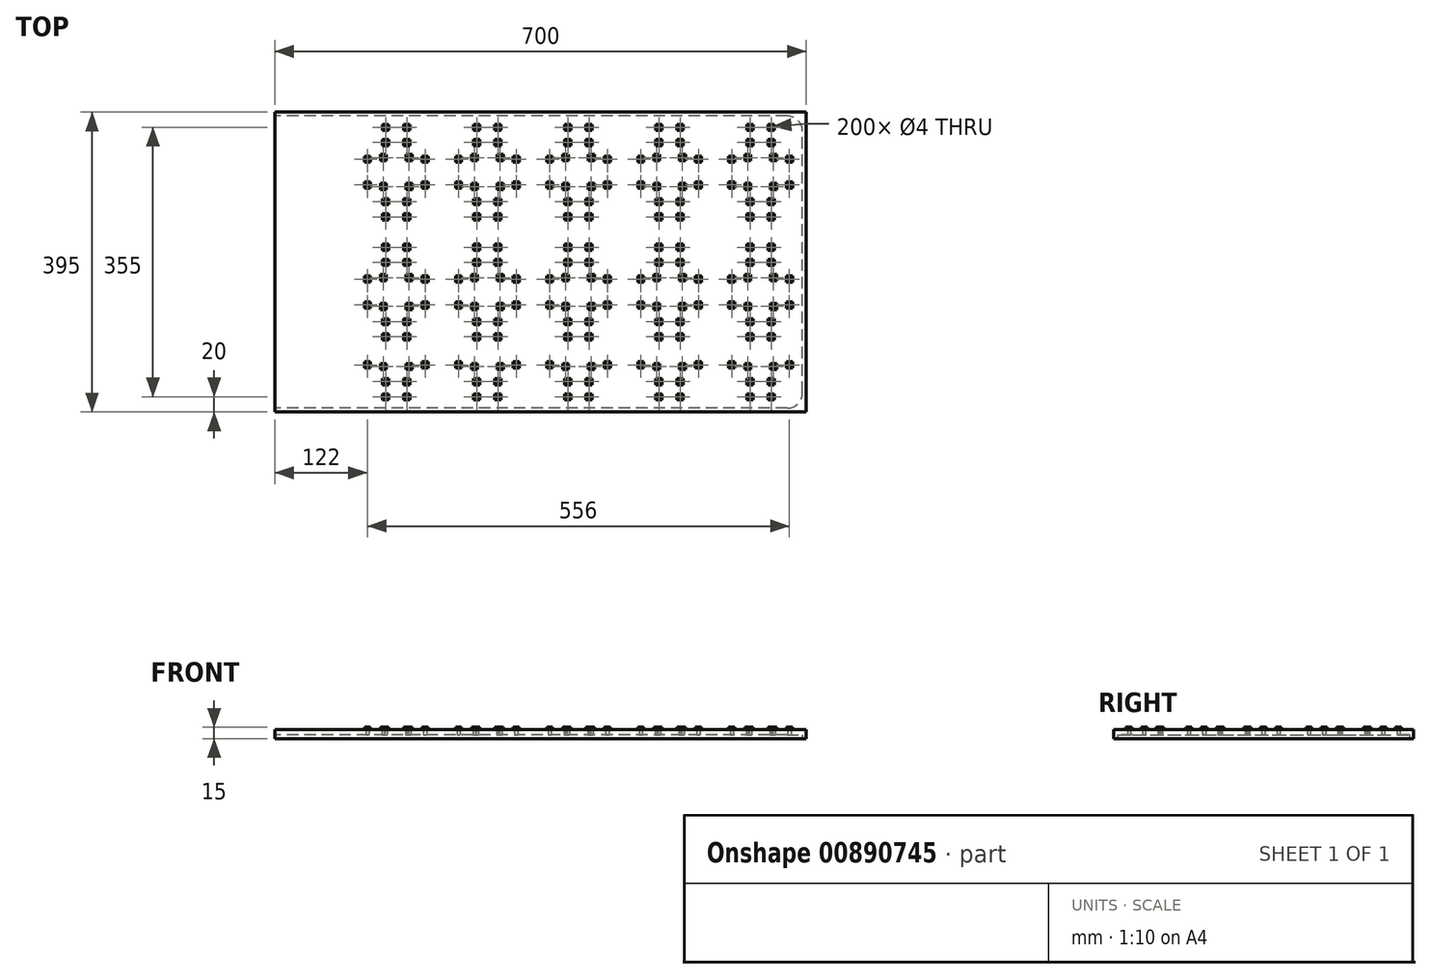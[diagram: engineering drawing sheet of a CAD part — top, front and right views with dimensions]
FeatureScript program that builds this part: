
annotation { "Feature Type Name" : "Feature", "Feature Type Description" : "" }
export const myFeature = defineFeature(function(context is Context, id is Id, definition is map)
    precondition{}
    {
        {
            var Q0;
            Q0=qCreatedBy(makeId("Top.planeOp"),FACE);
            var sketch = newSketch(context, id + "F0", { "sketchPlane" : qUnion([Q0])});
            skLineSegment(sketch, "E0.bottom", {"start": v(0, 0) * mm, "end": v(-700, 0) * mm});
            skLineSegment(sketch, "E0.top", {"start": v(0, 395) * mm, "end": v(-700, 395) * mm});
            skLineSegment(sketch, "E0.left", {"start": v(0, 0) * mm, "end": v(0, 395) * mm});
            skLineSegment(sketch, "E0.right", {"start": v(-700, 0) * mm, "end": v(-700, 395) * mm});
            skPoint(sketch, "E1", {"position": v(-46, 40) * mm});
            skPoint(sketch, "E2", {"position": v(-46, 20) * mm});
            skPoint(sketch, "E3", {"position": v(-43, 60) * mm});
            skPoint(sketch, "E4", {"position": v(-22, 62) * mm});
            skLineSegment(sketch, "E5", {"start": v(0, 79) * mm, "end": v(-60, 79) * mm, "construction": true});
            skLineSegment(sketch, "E6", {"start": v(-60, 79) * mm, "end": v(-60, 0) * mm, "construction": true});
            skLineSegment(sketch, "E7", {"start": v(0, 158) * mm, "end": v(-60, 158) * mm, "construction": true});
            skLineSegment(sketch, "E8", {"start": v(0, 237) * mm, "end": v(-60, 237) * mm, "construction": true});
            skLineSegment(sketch, "E9", {"start": v(0, 316) * mm, "end": v(-60, 316) * mm, "construction": true});
            skLineSegment(sketch, "E10.0.1.2", {"start": v(0, 395) * mm, "end": v(-60, 395) * mm});
            skPoint(sketch, "E10.0.1.3", {"position": v(-46, 119) * mm});
            skPoint(sketch, "E10.0.1.4", {"position": v(-43, 139) * mm});
            skPoint(sketch, "E10.0.1.5", {"position": v(-46, 99) * mm});
            skPoint(sketch, "E10.0.1.6", {"position": v(-22, 141) * mm});
            skLineSegment(sketch, "E10.direction1", {"start": v(-46, 20) * mm, "end": v(-21, 20) * mm, "construction": true});
            skLineSegment(sketch, "E10.direction2", {"start": v(-46, 20) * mm, "end": v(-46, 99) * mm, "construction": true});
            skPoint(sketch, "E11.MirrorP", {"position": v(-43, 177) * mm});
            skPoint(sketch, "E12.MirrorP", {"position": v(-46, 217) * mm});
            skPoint(sketch, "E13.MirrorP", {"position": v(-46, 197) * mm});
            skPoint(sketch, "E14.MirrorP", {"position": v(-22, 175) * mm});
            skPoint(sketch, "E15.MirrorP", {"position": v(-43, 297) * mm});
            skPoint(sketch, "E16.MirrorP", {"position": v(-43, 335) * mm});
            skPoint(sketch, "E17.MirrorP", {"position": v(-46, 257) * mm});
            skPoint(sketch, "E18.MirrorP", {"position": v(-46, 277) * mm});
            skPoint(sketch, "E19.MirrorP", {"position": v(-46, 375) * mm});
            skPoint(sketch, "E20.MirrorP", {"position": v(-46, 355) * mm});
            skPoint(sketch, "E21.MirrorP", {"position": v(-22, 299) * mm});
            skPoint(sketch, "E22.MirrorP", {"position": v(-22, 333) * mm});
            skPoint(sketch, "E23.MirrorP", {"position": v(-74, 40) * mm});
            skPoint(sketch, "E24.MirrorP", {"position": v(-98, 62) * mm});
            skPoint(sketch, "E25.MirrorP", {"position": v(-77, 60) * mm});
            skPoint(sketch, "E26.MirrorP", {"position": v(-74, 20) * mm});
            skPoint(sketch, "E27.MirrorP", {"position": v(-74, 99) * mm});
            skPoint(sketch, "E28.MirrorP", {"position": v(-74, 375) * mm});
            skPoint(sketch, "E29.MirrorP", {"position": v(-77, 177) * mm});
            skPoint(sketch, "E30.MirrorP", {"position": v(-77, 335) * mm});
            skPoint(sketch, "E31.MirrorP", {"position": v(-98, 141) * mm});
            skPoint(sketch, "E32.MirrorP", {"position": v(-74, 355) * mm});
            skPoint(sketch, "E33.MirrorP", {"position": v(-77, 297) * mm});
            skPoint(sketch, "E34.MirrorP", {"position": v(-74, 257) * mm});
            skPoint(sketch, "E35.MirrorP", {"position": v(-98, 333) * mm});
            skPoint(sketch, "E36.MirrorP", {"position": v(-74, 217) * mm});
            skPoint(sketch, "E37.MirrorP", {"position": v(-98, 299) * mm});
            skPoint(sketch, "E38.MirrorP", {"position": v(-74, 277) * mm});
            skPoint(sketch, "E39.MirrorP", {"position": v(-98, 175) * mm});
            skPoint(sketch, "E40.MirrorP", {"position": v(-77, 139) * mm});
            skPoint(sketch, "E41.MirrorP", {"position": v(-74, 119) * mm});
            skPoint(sketch, "E42.MirrorP", {"position": v(-74, 197) * mm});
            skPoint(sketch, "E43.1.0.0", {"position": v(-218, 299) * mm});
            skPoint(sketch, "E43.1.0.1", {"position": v(-142, 299) * mm});
            skPoint(sketch, "E43.1.0.2", {"position": v(-194, 40) * mm});
            skPoint(sketch, "E43.1.0.3", {"position": v(-218, 175) * mm});
            skPoint(sketch, "E43.1.0.4", {"position": v(-218, 333) * mm});
            skPoint(sketch, "E43.1.0.5", {"position": v(-166, 197) * mm});
            skPoint(sketch, "E43.1.0.6", {"position": v(-197, 297) * mm});
            skPoint(sketch, "E43.1.0.7", {"position": v(-197, 335) * mm});
            skPoint(sketch, "E43.1.0.8", {"position": v(-142, 333) * mm});
            skPoint(sketch, "E43.1.0.9", {"position": v(-194, 375) * mm});
            skPoint(sketch, "E43.1.0.10", {"position": v(-163, 60) * mm});
            skPoint(sketch, "E43.1.0.11", {"position": v(-194, 197) * mm});
            skPoint(sketch, "E43.1.0.12", {"position": v(-163, 297) * mm});
            skPoint(sketch, "E43.1.0.13", {"position": v(-166, 375) * mm});
            skPoint(sketch, "E43.1.0.14", {"position": v(-197, 60) * mm});
            skPoint(sketch, "E43.1.0.15", {"position": v(-197, 139) * mm});
            skPoint(sketch, "E43.1.0.16", {"position": v(-166, 99) * mm});
            skPoint(sketch, "E43.1.0.17", {"position": v(-163, 335) * mm});
            skPoint(sketch, "E43.1.0.18", {"position": v(-142, 141) * mm});
            skPoint(sketch, "E43.1.0.19", {"position": v(-163, 177) * mm});
            skPoint(sketch, "E43.1.0.20", {"position": v(-166, 40) * mm});
            skPoint(sketch, "E43.1.0.21", {"position": v(-194, 217) * mm});
            skPoint(sketch, "E43.1.0.22", {"position": v(-194, 99) * mm});
            skPoint(sketch, "E43.1.0.23", {"position": v(-163, 139) * mm});
            skPoint(sketch, "E43.1.0.24", {"position": v(-218, 62) * mm});
            skPoint(sketch, "E43.1.0.25", {"position": v(-197, 177) * mm});
            skPoint(sketch, "E43.1.0.26", {"position": v(-194, 20) * mm});
            skPoint(sketch, "E43.1.0.27", {"position": v(-142, 175) * mm});
            skPoint(sketch, "E43.1.0.28", {"position": v(-166, 257) * mm});
            skPoint(sketch, "E43.1.0.29", {"position": v(-194, 355) * mm});
            skPoint(sketch, "E43.1.0.30", {"position": v(-166, 355) * mm});
            skPoint(sketch, "E43.1.0.31", {"position": v(-194, 277) * mm});
            skPoint(sketch, "E43.1.0.32", {"position": v(-166, 20) * mm});
            skPoint(sketch, "E43.1.0.33", {"position": v(-194, 119) * mm});
            skPoint(sketch, "E43.1.0.34", {"position": v(-166, 217) * mm});
            skPoint(sketch, "E43.1.0.35", {"position": v(-142, 62) * mm});
            skPoint(sketch, "E43.1.0.36", {"position": v(-166, 119) * mm});
            skPoint(sketch, "E43.1.0.37", {"position": v(-218, 141) * mm});
            skPoint(sketch, "E43.1.0.38", {"position": v(-194, 257) * mm});
            skPoint(sketch, "E43.1.0.39", {"position": v(-166, 277) * mm});
            skPoint(sketch, "E43.2.0.0", {"position": v(-338, 299) * mm});
            skPoint(sketch, "E43.2.0.1", {"position": v(-262, 299) * mm});
            skPoint(sketch, "E43.2.0.2", {"position": v(-314, 40) * mm});
            skPoint(sketch, "E43.2.0.3", {"position": v(-338, 175) * mm});
            skPoint(sketch, "E43.2.0.4", {"position": v(-338, 333) * mm});
            skPoint(sketch, "E43.2.0.5", {"position": v(-286, 197) * mm});
            skPoint(sketch, "E43.2.0.6", {"position": v(-317, 297) * mm});
            skPoint(sketch, "E43.2.0.7", {"position": v(-317, 335) * mm});
            skPoint(sketch, "E43.2.0.8", {"position": v(-262, 333) * mm});
            skPoint(sketch, "E43.2.0.9", {"position": v(-314, 375) * mm});
            skPoint(sketch, "E43.2.0.10", {"position": v(-283, 60) * mm});
            skPoint(sketch, "E43.2.0.11", {"position": v(-314, 197) * mm});
            skPoint(sketch, "E43.2.0.12", {"position": v(-283, 297) * mm});
            skPoint(sketch, "E43.2.0.13", {"position": v(-286, 375) * mm});
            skPoint(sketch, "E43.2.0.14", {"position": v(-317, 60) * mm});
            skPoint(sketch, "E43.2.0.15", {"position": v(-317, 139) * mm});
            skPoint(sketch, "E43.2.0.16", {"position": v(-286, 99) * mm});
            skPoint(sketch, "E43.2.0.17", {"position": v(-283, 335) * mm});
            skPoint(sketch, "E43.2.0.18", {"position": v(-262, 141) * mm});
            skPoint(sketch, "E43.2.0.19", {"position": v(-283, 177) * mm});
            skPoint(sketch, "E43.2.0.20", {"position": v(-286, 40) * mm});
            skPoint(sketch, "E43.2.0.21", {"position": v(-314, 217) * mm});
            skPoint(sketch, "E43.2.0.22", {"position": v(-314, 99) * mm});
            skPoint(sketch, "E43.2.0.23", {"position": v(-283, 139) * mm});
            skPoint(sketch, "E43.2.0.24", {"position": v(-338, 62) * mm});
            skPoint(sketch, "E43.2.0.25", {"position": v(-317, 177) * mm});
            skPoint(sketch, "E43.2.0.26", {"position": v(-314, 20) * mm});
            skPoint(sketch, "E43.2.0.27", {"position": v(-262, 175) * mm});
            skPoint(sketch, "E43.2.0.28", {"position": v(-286, 257) * mm});
            skPoint(sketch, "E43.2.0.29", {"position": v(-314, 355) * mm});
            skPoint(sketch, "E43.2.0.30", {"position": v(-286, 355) * mm});
            skPoint(sketch, "E43.2.0.31", {"position": v(-314, 277) * mm});
            skPoint(sketch, "E43.2.0.32", {"position": v(-286, 20) * mm});
            skPoint(sketch, "E43.2.0.33", {"position": v(-314, 119) * mm});
            skPoint(sketch, "E43.2.0.34", {"position": v(-286, 217) * mm});
            skPoint(sketch, "E43.2.0.35", {"position": v(-262, 62) * mm});
            skPoint(sketch, "E43.2.0.36", {"position": v(-286, 119) * mm});
            skPoint(sketch, "E43.2.0.37", {"position": v(-338, 141) * mm});
            skPoint(sketch, "E43.2.0.38", {"position": v(-314, 257) * mm});
            skPoint(sketch, "E43.2.0.39", {"position": v(-286, 277) * mm});
            skPoint(sketch, "E43.3.0.0", {"position": v(-458, 299) * mm});
            skPoint(sketch, "E43.3.0.1", {"position": v(-382, 299) * mm});
            skPoint(sketch, "E43.3.0.2", {"position": v(-434, 40) * mm});
            skPoint(sketch, "E43.3.0.3", {"position": v(-458, 175) * mm});
            skPoint(sketch, "E43.3.0.4", {"position": v(-458, 333) * mm});
            skPoint(sketch, "E43.3.0.5", {"position": v(-406, 197) * mm});
            skPoint(sketch, "E43.3.0.6", {"position": v(-437, 297) * mm});
            skPoint(sketch, "E43.3.0.7", {"position": v(-437, 335) * mm});
            skPoint(sketch, "E43.3.0.8", {"position": v(-382, 333) * mm});
            skPoint(sketch, "E43.3.0.9", {"position": v(-434, 375) * mm});
            skPoint(sketch, "E43.3.0.10", {"position": v(-403, 60) * mm});
            skPoint(sketch, "E43.3.0.11", {"position": v(-434, 197) * mm});
            skPoint(sketch, "E43.3.0.12", {"position": v(-403, 297) * mm});
            skPoint(sketch, "E43.3.0.13", {"position": v(-406, 375) * mm});
            skPoint(sketch, "E43.3.0.14", {"position": v(-437, 60) * mm});
            skPoint(sketch, "E43.3.0.15", {"position": v(-437, 139) * mm});
            skPoint(sketch, "E43.3.0.16", {"position": v(-406, 99) * mm});
            skPoint(sketch, "E43.3.0.17", {"position": v(-403, 335) * mm});
            skPoint(sketch, "E43.3.0.18", {"position": v(-382, 141) * mm});
            skPoint(sketch, "E43.3.0.19", {"position": v(-403, 177) * mm});
            skPoint(sketch, "E43.3.0.20", {"position": v(-406, 40) * mm});
            skPoint(sketch, "E43.3.0.21", {"position": v(-434, 217) * mm});
            skPoint(sketch, "E43.3.0.22", {"position": v(-434, 99) * mm});
            skPoint(sketch, "E43.3.0.23", {"position": v(-403, 139) * mm});
            skPoint(sketch, "E43.3.0.24", {"position": v(-458, 62) * mm});
            skPoint(sketch, "E43.3.0.25", {"position": v(-437, 177) * mm});
            skPoint(sketch, "E43.3.0.26", {"position": v(-434, 20) * mm});
            skPoint(sketch, "E43.3.0.27", {"position": v(-382, 175) * mm});
            skPoint(sketch, "E43.3.0.28", {"position": v(-406, 257) * mm});
            skPoint(sketch, "E43.3.0.29", {"position": v(-434, 355) * mm});
            skPoint(sketch, "E43.3.0.30", {"position": v(-406, 355) * mm});
            skPoint(sketch, "E43.3.0.31", {"position": v(-434, 277) * mm});
            skPoint(sketch, "E43.3.0.32", {"position": v(-406, 20) * mm});
            skPoint(sketch, "E43.3.0.33", {"position": v(-434, 119) * mm});
            skPoint(sketch, "E43.3.0.34", {"position": v(-406, 217) * mm});
            skPoint(sketch, "E43.3.0.35", {"position": v(-382, 62) * mm});
            skPoint(sketch, "E43.3.0.36", {"position": v(-406, 119) * mm});
            skPoint(sketch, "E43.3.0.37", {"position": v(-458, 141) * mm});
            skPoint(sketch, "E43.3.0.38", {"position": v(-434, 257) * mm});
            skPoint(sketch, "E43.3.0.39", {"position": v(-406, 277) * mm});
            skPoint(sketch, "E43.4.0.0", {"position": v(-578, 299) * mm});
            skPoint(sketch, "E43.4.0.1", {"position": v(-502, 299) * mm});
            skPoint(sketch, "E43.4.0.2", {"position": v(-554, 40) * mm});
            skPoint(sketch, "E43.4.0.3", {"position": v(-578, 175) * mm});
            skPoint(sketch, "E43.4.0.4", {"position": v(-578, 333) * mm});
            skPoint(sketch, "E43.4.0.5", {"position": v(-526, 197) * mm});
            skPoint(sketch, "E43.4.0.6", {"position": v(-557, 297) * mm});
            skPoint(sketch, "E43.4.0.7", {"position": v(-557, 335) * mm});
            skPoint(sketch, "E43.4.0.8", {"position": v(-502, 333) * mm});
            skPoint(sketch, "E43.4.0.9", {"position": v(-554, 375) * mm});
            skPoint(sketch, "E43.4.0.10", {"position": v(-523, 60) * mm});
            skPoint(sketch, "E43.4.0.11", {"position": v(-554, 197) * mm});
            skPoint(sketch, "E43.4.0.12", {"position": v(-523, 297) * mm});
            skPoint(sketch, "E43.4.0.13", {"position": v(-526, 375) * mm});
            skPoint(sketch, "E43.4.0.14", {"position": v(-557, 60) * mm});
            skPoint(sketch, "E43.4.0.15", {"position": v(-557, 139) * mm});
            skPoint(sketch, "E43.4.0.16", {"position": v(-526, 99) * mm});
            skPoint(sketch, "E43.4.0.17", {"position": v(-523, 335) * mm});
            skPoint(sketch, "E43.4.0.18", {"position": v(-502, 141) * mm});
            skPoint(sketch, "E43.4.0.19", {"position": v(-523, 177) * mm});
            skPoint(sketch, "E43.4.0.20", {"position": v(-526, 40) * mm});
            skPoint(sketch, "E43.4.0.21", {"position": v(-554, 217) * mm});
            skPoint(sketch, "E43.4.0.22", {"position": v(-554, 99) * mm});
            skPoint(sketch, "E43.4.0.23", {"position": v(-523, 139) * mm});
            skPoint(sketch, "E43.4.0.24", {"position": v(-578, 62) * mm});
            skPoint(sketch, "E43.4.0.25", {"position": v(-557, 177) * mm});
            skPoint(sketch, "E43.4.0.26", {"position": v(-554, 20) * mm});
            skPoint(sketch, "E43.4.0.27", {"position": v(-502, 175) * mm});
            skPoint(sketch, "E43.4.0.28", {"position": v(-526, 257) * mm});
            skPoint(sketch, "E43.4.0.29", {"position": v(-554, 355) * mm});
            skPoint(sketch, "E43.4.0.30", {"position": v(-526, 355) * mm});
            skPoint(sketch, "E43.4.0.31", {"position": v(-554, 277) * mm});
            skPoint(sketch, "E43.4.0.32", {"position": v(-526, 20) * mm});
            skPoint(sketch, "E43.4.0.33", {"position": v(-554, 119) * mm});
            skPoint(sketch, "E43.4.0.34", {"position": v(-526, 217) * mm});
            skPoint(sketch, "E43.4.0.35", {"position": v(-502, 62) * mm});
            skPoint(sketch, "E43.4.0.36", {"position": v(-526, 119) * mm});
            skPoint(sketch, "E43.4.0.37", {"position": v(-578, 141) * mm});
            skPoint(sketch, "E43.4.0.38", {"position": v(-554, 257) * mm});
            skPoint(sketch, "E43.4.0.39", {"position": v(-526, 277) * mm});
            skLineSegment(sketch, "E43.direction1", {"start": v(-74, 20) * mm, "end": v(-194, 20) * mm, "construction": true});
            skSolve(sketch);
        }
        {
            var Q0;
            Q0 = qSketchRegion(id + "F0", true);
            extrude(context, id + "F1", {"entities" : qUnion([Q0]), "depth" : 12 * mm, "offsetDistance" : 25 * mm});
        }
        {
            var Q0;
            Q0=makeQuery(id+"F0.imprint","IMPRINT",FACE,{"disambiguationData":[TD([[makeQuery(id+"F0.imprint","IMPRINT",EDGE,{"derivedFrom":sQuery(id+"F0.wireOp",EDGE,"E0.bottom")}),-1.0]])]});
            var sketch = newSketch(context, id + "F2", { "sketchPlane" : qUnion([Q0])});
            skLineSegment(sketch, "E44.bottom", {"start": v(-18, 66) * mm, "end": v(-26, 66) * mm});
            skLineSegment(sketch, "E44.top", {"start": v(-18, 58) * mm, "end": v(-26, 58) * mm});
            skLineSegment(sketch, "E44.left", {"start": v(-18, 66) * mm, "end": v(-18, 58) * mm});
            skLineSegment(sketch, "E44.right", {"start": v(-26, 66) * mm, "end": v(-26, 58) * mm});
            skPoint(sketch, "E44.middle", {"position": v(-22, 62) * mm});
            skLineSegment(sketch, "E45.bottom", {"start": v(-42, 24) * mm, "end": v(-50, 24) * mm});
            skLineSegment(sketch, "E45.top", {"start": v(-42, 16) * mm, "end": v(-50, 16) * mm});
            skLineSegment(sketch, "E45.left", {"start": v(-42, 24) * mm, "end": v(-42, 16) * mm});
            skLineSegment(sketch, "E45.right", {"start": v(-50, 24) * mm, "end": v(-50, 16) * mm});
            skPoint(sketch, "E45.middle", {"position": v(-46, 20) * mm});
            skLineSegment(sketch, "E46.bottom", {"start": v(-42, 44) * mm, "end": v(-50, 44) * mm});
            skLineSegment(sketch, "E46.top", {"start": v(-42, 36) * mm, "end": v(-50, 36) * mm});
            skLineSegment(sketch, "E46.left", {"start": v(-42, 44) * mm, "end": v(-42, 36) * mm});
            skLineSegment(sketch, "E46.right", {"start": v(-50, 44) * mm, "end": v(-50, 36) * mm});
            skPoint(sketch, "E46.middle", {"position": v(-46, 40) * mm});
            skLineSegment(sketch, "E47.bottom", {"start": v(-39, 64) * mm, "end": v(-47, 64) * mm});
            skLineSegment(sketch, "E47.top", {"start": v(-39, 56) * mm, "end": v(-47, 56) * mm});
            skLineSegment(sketch, "E47.left", {"start": v(-39, 64) * mm, "end": v(-39, 56) * mm});
            skLineSegment(sketch, "E47.right", {"start": v(-47, 64) * mm, "end": v(-47, 56) * mm});
            skPoint(sketch, "E47.middle", {"position": v(-43, 60) * mm});
            skLineSegment(sketch, "E48.bottom", {"start": v(-42, 103) * mm, "end": v(-50, 103) * mm});
            skLineSegment(sketch, "E48.top", {"start": v(-42, 95) * mm, "end": v(-50, 95) * mm});
            skLineSegment(sketch, "E48.left", {"start": v(-42, 103) * mm, "end": v(-42, 95) * mm});
            skLineSegment(sketch, "E48.right", {"start": v(-50, 103) * mm, "end": v(-50, 95) * mm});
            skPoint(sketch, "E48.middle", {"position": v(-46, 99) * mm});
            skLineSegment(sketch, "E49.bottom", {"start": v(-42, 123) * mm, "end": v(-50, 123) * mm});
            skLineSegment(sketch, "E49.top", {"start": v(-42, 115) * mm, "end": v(-50, 115) * mm});
            skLineSegment(sketch, "E49.left", {"start": v(-42, 123) * mm, "end": v(-42, 115) * mm});
            skLineSegment(sketch, "E49.right", {"start": v(-50, 123) * mm, "end": v(-50, 115) * mm});
            skPoint(sketch, "E49.middle", {"position": v(-46, 119) * mm});
            skLineSegment(sketch, "E50.bottom", {"start": v(-39, 143) * mm, "end": v(-47, 143) * mm});
            skLineSegment(sketch, "E50.top", {"start": v(-39, 135) * mm, "end": v(-47, 135) * mm});
            skLineSegment(sketch, "E50.left", {"start": v(-39, 143) * mm, "end": v(-39, 135) * mm});
            skLineSegment(sketch, "E50.right", {"start": v(-47, 143) * mm, "end": v(-47, 135) * mm});
            skPoint(sketch, "E50.middle", {"position": v(-43, 139) * mm});
            skLineSegment(sketch, "E51.bottom", {"start": v(-18, 145) * mm, "end": v(-26, 145) * mm});
            skLineSegment(sketch, "E51.top", {"start": v(-18, 137) * mm, "end": v(-26, 137) * mm});
            skLineSegment(sketch, "E51.left", {"start": v(-18, 145) * mm, "end": v(-18, 137) * mm});
            skLineSegment(sketch, "E51.right", {"start": v(-26, 145) * mm, "end": v(-26, 137) * mm});
            skPoint(sketch, "E51.middle", {"position": v(-22, 141) * mm});
            skLineSegment(sketch, "E52.bottom", {"start": v(-18, 179) * mm, "end": v(-26, 179) * mm});
            skLineSegment(sketch, "E52.top", {"start": v(-18, 171) * mm, "end": v(-26, 171) * mm});
            skLineSegment(sketch, "E52.left", {"start": v(-18, 179) * mm, "end": v(-18, 171) * mm});
            skLineSegment(sketch, "E52.right", {"start": v(-26, 179) * mm, "end": v(-26, 171) * mm});
            skPoint(sketch, "E52.middle", {"position": v(-22, 175) * mm});
            skLineSegment(sketch, "E53.bottom", {"start": v(-39, 181) * mm, "end": v(-47, 181) * mm});
            skLineSegment(sketch, "E53.top", {"start": v(-39, 173) * mm, "end": v(-47, 173) * mm});
            skLineSegment(sketch, "E53.left", {"start": v(-39, 181) * mm, "end": v(-39, 173) * mm});
            skLineSegment(sketch, "E53.right", {"start": v(-47, 181) * mm, "end": v(-47, 173) * mm});
            skPoint(sketch, "E53.middle", {"position": v(-43, 177) * mm});
            skLineSegment(sketch, "E54.bottom", {"start": v(-42, 201) * mm, "end": v(-50, 201) * mm});
            skLineSegment(sketch, "E54.top", {"start": v(-42, 193) * mm, "end": v(-50, 193) * mm});
            skLineSegment(sketch, "E54.left", {"start": v(-42, 201) * mm, "end": v(-42, 193) * mm});
            skLineSegment(sketch, "E54.right", {"start": v(-50, 201) * mm, "end": v(-50, 193) * mm});
            skPoint(sketch, "E54.middle", {"position": v(-46, 197) * mm});
            skLineSegment(sketch, "E55.bottom", {"start": v(-42, 221) * mm, "end": v(-50, 221) * mm});
            skLineSegment(sketch, "E55.top", {"start": v(-42, 213) * mm, "end": v(-50, 213) * mm});
            skLineSegment(sketch, "E55.left", {"start": v(-42, 221) * mm, "end": v(-42, 213) * mm});
            skLineSegment(sketch, "E55.right", {"start": v(-50, 221) * mm, "end": v(-50, 213) * mm});
            skPoint(sketch, "E55.middle", {"position": v(-46, 217) * mm});
            skLineSegment(sketch, "E56.bottom", {"start": v(-42, 261) * mm, "end": v(-50, 261) * mm});
            skLineSegment(sketch, "E56.top", {"start": v(-42, 253) * mm, "end": v(-50, 253) * mm});
            skLineSegment(sketch, "E56.left", {"start": v(-42, 261) * mm, "end": v(-42, 253) * mm});
            skLineSegment(sketch, "E56.right", {"start": v(-50, 261) * mm, "end": v(-50, 253) * mm});
            skPoint(sketch, "E56.middle", {"position": v(-46, 257) * mm});
            skLineSegment(sketch, "E57.bottom", {"start": v(-42, 281) * mm, "end": v(-50, 281) * mm});
            skLineSegment(sketch, "E57.top", {"start": v(-42, 273) * mm, "end": v(-50, 273) * mm});
            skLineSegment(sketch, "E57.left", {"start": v(-42, 281) * mm, "end": v(-42, 273) * mm});
            skLineSegment(sketch, "E57.right", {"start": v(-50, 281) * mm, "end": v(-50, 273) * mm});
            skPoint(sketch, "E57.middle", {"position": v(-46, 277) * mm});
            skLineSegment(sketch, "E58.bottom", {"start": v(-39, 301) * mm, "end": v(-47, 301) * mm});
            skLineSegment(sketch, "E58.top", {"start": v(-39, 293) * mm, "end": v(-47, 293) * mm});
            skLineSegment(sketch, "E58.left", {"start": v(-39, 301) * mm, "end": v(-39, 293) * mm});
            skLineSegment(sketch, "E58.right", {"start": v(-47, 301) * mm, "end": v(-47, 293) * mm});
            skPoint(sketch, "E58.middle", {"position": v(-43, 297) * mm});
            skLineSegment(sketch, "E59.bottom", {"start": v(-18, 303) * mm, "end": v(-26, 303) * mm});
            skLineSegment(sketch, "E59.top", {"start": v(-18, 295) * mm, "end": v(-26, 295) * mm});
            skLineSegment(sketch, "E59.left", {"start": v(-18, 303) * mm, "end": v(-18, 295) * mm});
            skLineSegment(sketch, "E59.right", {"start": v(-26, 303) * mm, "end": v(-26, 295) * mm});
            skPoint(sketch, "E59.middle", {"position": v(-22, 299) * mm});
            skLineSegment(sketch, "E60.bottom", {"start": v(-18, 337) * mm, "end": v(-26, 337) * mm});
            skLineSegment(sketch, "E60.top", {"start": v(-18, 329) * mm, "end": v(-26, 329) * mm});
            skLineSegment(sketch, "E60.left", {"start": v(-18, 337) * mm, "end": v(-18, 329) * mm});
            skLineSegment(sketch, "E60.right", {"start": v(-26, 337) * mm, "end": v(-26, 329) * mm});
            skPoint(sketch, "E60.middle", {"position": v(-22, 333) * mm});
            skLineSegment(sketch, "E61.bottom", {"start": v(-39, 339) * mm, "end": v(-47, 339) * mm});
            skLineSegment(sketch, "E61.top", {"start": v(-39, 331) * mm, "end": v(-47, 331) * mm});
            skLineSegment(sketch, "E61.left", {"start": v(-39, 339) * mm, "end": v(-39, 331) * mm});
            skLineSegment(sketch, "E61.right", {"start": v(-47, 339) * mm, "end": v(-47, 331) * mm});
            skPoint(sketch, "E61.middle", {"position": v(-43, 335) * mm});
            skLineSegment(sketch, "E62.bottom", {"start": v(-42, 359) * mm, "end": v(-50, 359) * mm});
            skLineSegment(sketch, "E62.top", {"start": v(-42, 351) * mm, "end": v(-50, 351) * mm});
            skLineSegment(sketch, "E62.left", {"start": v(-42, 359) * mm, "end": v(-42, 351) * mm});
            skLineSegment(sketch, "E62.right", {"start": v(-50, 359) * mm, "end": v(-50, 351) * mm});
            skPoint(sketch, "E62.middle", {"position": v(-46, 355) * mm});
            skLineSegment(sketch, "E63.bottom", {"start": v(-42, 379) * mm, "end": v(-50, 379) * mm});
            skLineSegment(sketch, "E63.top", {"start": v(-42, 371) * mm, "end": v(-50, 371) * mm});
            skLineSegment(sketch, "E63.left", {"start": v(-42, 379) * mm, "end": v(-42, 371) * mm});
            skLineSegment(sketch, "E63.right", {"start": v(-50, 379) * mm, "end": v(-50, 371) * mm});
            skPoint(sketch, "E63.middle", {"position": v(-46, 375) * mm});
            skLineSegment(sketch, "E64.MirrorCS", {"start": v(-81, 143) * mm, "end": v(-73, 143) * mm});
            skLineSegment(sketch, "E65.MirrorCS", {"start": v(-81, 301) * mm, "end": v(-73, 301) * mm});
            skLineSegment(sketch, "E66.MirrorCS", {"start": v(-78, 281) * mm, "end": v(-70, 281) * mm});
            skLineSegment(sketch, "E67.MirrorCS", {"start": v(-81, 143) * mm, "end": v(-81, 135) * mm});
            skLineSegment(sketch, "E68.MirrorCS", {"start": v(-70, 44) * mm, "end": v(-70, 36) * mm});
            skLineSegment(sketch, "E69.MirrorCS", {"start": v(-81, 135) * mm, "end": v(-73, 135) * mm});
            skLineSegment(sketch, "E70.MirrorCS", {"start": v(-70, 281) * mm, "end": v(-70, 273) * mm});
            skLineSegment(sketch, "E71.MirrorCS", {"start": v(-78, 281) * mm, "end": v(-78, 273) * mm});
            skLineSegment(sketch, "E72.MirrorCS", {"start": v(-78, 44) * mm, "end": v(-70, 44) * mm});
            skLineSegment(sketch, "E73.MirrorCS", {"start": v(-78, 273) * mm, "end": v(-70, 273) * mm});
            skLineSegment(sketch, "E74.MirrorCS", {"start": v(-78, 36) * mm, "end": v(-70, 36) * mm});
            skLineSegment(sketch, "E75.MirrorCS", {"start": v(-78, 44) * mm, "end": v(-78, 36) * mm});
            skLineSegment(sketch, "E76.MirrorCS", {"start": v(-73, 143) * mm, "end": v(-73, 135) * mm});
            skLineSegment(sketch, "E77.MirrorCS", {"start": v(-81, 293) * mm, "end": v(-73, 293) * mm});
            skLineSegment(sketch, "E78.MirrorCS", {"start": v(-73, 301) * mm, "end": v(-73, 293) * mm});
            skLineSegment(sketch, "E79.MirrorCS", {"start": v(-81, 301) * mm, "end": v(-81, 293) * mm});
            skLineSegment(sketch, "E80.MirrorCS", {"start": v(-78, 253) * mm, "end": v(-70, 253) * mm});
            skLineSegment(sketch, "E81.MirrorCS", {"start": v(-70, 221) * mm, "end": v(-70, 213) * mm});
            skLineSegment(sketch, "E82.MirrorCS", {"start": v(-78, 261) * mm, "end": v(-70, 261) * mm});
            skLineSegment(sketch, "E83.MirrorCS", {"start": v(-70, 201) * mm, "end": v(-70, 193) * mm});
            skLineSegment(sketch, "E84.MirrorCS", {"start": v(-78, 123) * mm, "end": v(-78, 115) * mm});
            skLineSegment(sketch, "E85.MirrorCS", {"start": v(-78, 371) * mm, "end": v(-70, 371) * mm});
            skLineSegment(sketch, "E86.MirrorCS", {"start": v(-81, 339) * mm, "end": v(-73, 339) * mm});
            skLineSegment(sketch, "E87.MirrorCS", {"start": v(-81, 181) * mm, "end": v(-73, 181) * mm});
            skLineSegment(sketch, "E88.MirrorCS", {"start": v(-78, 351) * mm, "end": v(-70, 351) * mm});
            skLineSegment(sketch, "E89.MirrorCS", {"start": v(-78, 379) * mm, "end": v(-70, 379) * mm});
            skLineSegment(sketch, "E90.MirrorCS", {"start": v(-81, 56) * mm, "end": v(-73, 56) * mm});
            skLineSegment(sketch, "E91.MirrorCS", {"start": v(-81, 331) * mm, "end": v(-73, 331) * mm});
            skLineSegment(sketch, "E92.MirrorCS", {"start": v(-78, 201) * mm, "end": v(-70, 201) * mm});
            skLineSegment(sketch, "E93.MirrorCS", {"start": v(-73, 339) * mm, "end": v(-73, 331) * mm});
            skLineSegment(sketch, "E94.MirrorCS", {"start": v(-70, 24) * mm, "end": v(-70, 16) * mm});
            skLineSegment(sketch, "E95.MirrorCS", {"start": v(-78, 24) * mm, "end": v(-78, 16) * mm});
            skLineSegment(sketch, "E96.MirrorCS", {"start": v(-78, 213) * mm, "end": v(-70, 213) * mm});
            skLineSegment(sketch, "E97.MirrorCS", {"start": v(-78, 103) * mm, "end": v(-78, 95) * mm});
            skLineSegment(sketch, "E98.MirrorCS", {"start": v(-78, 261) * mm, "end": v(-78, 253) * mm});
            skLineSegment(sketch, "E99.MirrorCS", {"start": v(-78, 115) * mm, "end": v(-70, 115) * mm});
            skLineSegment(sketch, "E100.MirrorCS", {"start": v(-81, 173) * mm, "end": v(-73, 173) * mm});
            skLineSegment(sketch, "E101.MirrorCS", {"start": v(-70, 359) * mm, "end": v(-70, 351) * mm});
            skLineSegment(sketch, "E102.MirrorCS", {"start": v(-78, 103) * mm, "end": v(-70, 103) * mm});
            skLineSegment(sketch, "E103.MirrorCS", {"start": v(-70, 123) * mm, "end": v(-70, 115) * mm});
            skLineSegment(sketch, "E104.MirrorCS", {"start": v(-73, 64) * mm, "end": v(-73, 56) * mm});
            skLineSegment(sketch, "E105.MirrorCS", {"start": v(-78, 123) * mm, "end": v(-70, 123) * mm});
            skLineSegment(sketch, "E106.MirrorCS", {"start": v(-70, 379) * mm, "end": v(-70, 371) * mm});
            skLineSegment(sketch, "E107.MirrorCS", {"start": v(-78, 201) * mm, "end": v(-78, 193) * mm});
            skLineSegment(sketch, "E108.MirrorCS", {"start": v(-73, 181) * mm, "end": v(-73, 173) * mm});
            skLineSegment(sketch, "E109.MirrorCS", {"start": v(-78, 359) * mm, "end": v(-70, 359) * mm});
            skLineSegment(sketch, "E110.MirrorCS", {"start": v(-78, 379) * mm, "end": v(-78, 371) * mm});
            skLineSegment(sketch, "E111.MirrorCS", {"start": v(-78, 193) * mm, "end": v(-70, 193) * mm});
            skLineSegment(sketch, "E112.MirrorCS", {"start": v(-70, 261) * mm, "end": v(-70, 253) * mm});
            skLineSegment(sketch, "E113.MirrorCS", {"start": v(-81, 181) * mm, "end": v(-81, 173) * mm});
            skLineSegment(sketch, "E114.MirrorCS", {"start": v(-81, 64) * mm, "end": v(-81, 56) * mm});
            skLineSegment(sketch, "E115.MirrorCS", {"start": v(-78, 359) * mm, "end": v(-78, 351) * mm});
            skLineSegment(sketch, "E116.MirrorCS", {"start": v(-81, 64) * mm, "end": v(-73, 64) * mm});
            skLineSegment(sketch, "E117.MirrorCS", {"start": v(-78, 221) * mm, "end": v(-70, 221) * mm});
            skLineSegment(sketch, "E118.MirrorCS", {"start": v(-81, 339) * mm, "end": v(-81, 331) * mm});
            skLineSegment(sketch, "E119.MirrorCS", {"start": v(-70, 103) * mm, "end": v(-70, 95) * mm});
            skLineSegment(sketch, "E120.MirrorCS", {"start": v(-78, 16) * mm, "end": v(-70, 16) * mm});
            skLineSegment(sketch, "E121.MirrorCS", {"start": v(-78, 95) * mm, "end": v(-70, 95) * mm});
            skLineSegment(sketch, "E122.MirrorCS", {"start": v(-78, 24) * mm, "end": v(-70, 24) * mm});
            skLineSegment(sketch, "E123.MirrorCS", {"start": v(-78, 221) * mm, "end": v(-78, 213) * mm});
            skLineSegment(sketch, "E124.MirrorCS", {"start": v(-102, 145) * mm, "end": v(-94, 145) * mm});
            skLineSegment(sketch, "E125.MirrorCS", {"start": v(-102, 337) * mm, "end": v(-102, 329) * mm});
            skLineSegment(sketch, "E126.MirrorCS", {"start": v(-102, 337) * mm, "end": v(-94, 337) * mm});
            skLineSegment(sketch, "E127.MirrorCS", {"start": v(-102, 303) * mm, "end": v(-94, 303) * mm});
            skLineSegment(sketch, "E128.MirrorCS", {"start": v(-102, 66) * mm, "end": v(-94, 66) * mm});
            skLineSegment(sketch, "E129.MirrorCS", {"start": v(-102, 171) * mm, "end": v(-94, 171) * mm});
            skLineSegment(sketch, "E130.MirrorCS", {"start": v(-102, 145) * mm, "end": v(-102, 137) * mm});
            skLineSegment(sketch, "E131.MirrorCS", {"start": v(-102, 295) * mm, "end": v(-94, 295) * mm});
            skLineSegment(sketch, "E132.MirrorCS", {"start": v(-94, 337) * mm, "end": v(-94, 329) * mm});
            skLineSegment(sketch, "E133.MirrorCS", {"start": v(-94, 145) * mm, "end": v(-94, 137) * mm});
            skLineSegment(sketch, "E134.MirrorCS", {"start": v(-102, 137) * mm, "end": v(-94, 137) * mm});
            skLineSegment(sketch, "E135.MirrorCS", {"start": v(-94, 179) * mm, "end": v(-94, 171) * mm});
            skLineSegment(sketch, "E136.MirrorCS", {"start": v(-102, 303) * mm, "end": v(-102, 295) * mm});
            skLineSegment(sketch, "E137.MirrorCS", {"start": v(-102, 179) * mm, "end": v(-102, 171) * mm});
            skLineSegment(sketch, "E138.MirrorCS", {"start": v(-94, 303) * mm, "end": v(-94, 295) * mm});
            skLineSegment(sketch, "E139.MirrorCS", {"start": v(-102, 66) * mm, "end": v(-102, 58) * mm});
            skLineSegment(sketch, "E140.MirrorCS", {"start": v(-102, 58) * mm, "end": v(-94, 58) * mm});
            skLineSegment(sketch, "E141.MirrorCS", {"start": v(-102, 179) * mm, "end": v(-94, 179) * mm});
            skLineSegment(sketch, "E142.MirrorCS", {"start": v(-94, 66) * mm, "end": v(-94, 58) * mm});
            skLineSegment(sketch, "E143.MirrorCS", {"start": v(-102, 329) * mm, "end": v(-94, 329) * mm});
            skPoint(sketch, "E144.MirrorP", {"position": v(-74, 40) * mm});
            skPoint(sketch, "E145.MirrorP", {"position": v(-74, 277) * mm});
            skPoint(sketch, "E146.MirrorP", {"position": v(-77, 297) * mm});
            skPoint(sketch, "E147.MirrorP", {"position": v(-77, 139) * mm});
            skPoint(sketch, "E148.MirrorP", {"position": v(-77, 60) * mm});
            skPoint(sketch, "E149.MirrorP", {"position": v(-77, 177) * mm});
            skPoint(sketch, "E150.MirrorP", {"position": v(-74, 20) * mm});
            skPoint(sketch, "E151.MirrorP", {"position": v(-98, 62) * mm});
            skPoint(sketch, "E152.MirrorP", {"position": v(-74, 355) * mm});
            skPoint(sketch, "E153.MirrorP", {"position": v(-98, 175) * mm});
            skPoint(sketch, "E154.MirrorP", {"position": v(-98, 141) * mm});
            skPoint(sketch, "E155.MirrorP", {"position": v(-74, 197) * mm});
            skPoint(sketch, "E156.MirrorP", {"position": v(-77, 335) * mm});
            skPoint(sketch, "E157.MirrorP", {"position": v(-98, 333) * mm});
            skPoint(sketch, "E158.MirrorP", {"position": v(-98, 299) * mm});
            skPoint(sketch, "E159.MirrorP", {"position": v(-74, 119) * mm});
            skPoint(sketch, "E160.MirrorP", {"position": v(-74, 257) * mm});
            skPoint(sketch, "E161.MirrorP", {"position": v(-74, 99) * mm});
            skPoint(sketch, "E162.MirrorP", {"position": v(-74, 375) * mm});
            skPoint(sketch, "E163.MirrorP", {"position": v(-74, 217) * mm});
            skPoint(sketch, "E164.1.0.0", {"position": v(-166, 197) * mm});
            skPoint(sketch, "E164.1.0.1", {"position": v(-194, 119) * mm});
            skPoint(sketch, "E164.1.0.2", {"position": v(-166, 119) * mm});
            skPoint(sketch, "E164.1.0.3", {"position": v(-142, 175) * mm});
            skPoint(sketch, "E164.1.0.4", {"position": v(-218, 299) * mm});
            skPoint(sketch, "E164.1.0.5", {"position": v(-218, 141) * mm});
            skPoint(sketch, "E164.1.0.6", {"position": v(-194, 217) * mm});
            skPoint(sketch, "E164.1.0.7", {"position": v(-194, 375) * mm});
            skPoint(sketch, "E164.1.0.8", {"position": v(-197, 60) * mm});
            skPoint(sketch, "E164.1.0.9", {"position": v(-218, 333) * mm});
            skPoint(sketch, "E164.1.0.10", {"position": v(-163, 335) * mm});
            skPoint(sketch, "E164.1.0.11", {"position": v(-194, 99) * mm});
            skPoint(sketch, "E164.1.0.12", {"position": v(-142, 333) * mm});
            skPoint(sketch, "E164.1.0.13", {"position": v(-194, 277) * mm});
            skPoint(sketch, "E164.1.0.14", {"position": v(-166, 217) * mm});
            skPoint(sketch, "E164.1.0.15", {"position": v(-194, 257) * mm});
            skPoint(sketch, "E164.1.0.16", {"position": v(-218, 175) * mm});
            skPoint(sketch, "E164.1.0.17", {"position": v(-166, 40) * mm});
            skPoint(sketch, "E164.1.0.18", {"position": v(-163, 60) * mm});
            skPoint(sketch, "E164.1.0.19", {"position": v(-218, 62) * mm});
            skPoint(sketch, "E164.1.0.20", {"position": v(-163, 177) * mm});
            skPoint(sketch, "E164.1.0.21", {"position": v(-166, 99) * mm});
            skPoint(sketch, "E164.1.0.22", {"position": v(-197, 177) * mm});
            skPoint(sketch, "E164.1.0.23", {"position": v(-194, 355) * mm});
            skPoint(sketch, "E164.1.0.24", {"position": v(-194, 197) * mm});
            skPoint(sketch, "E164.1.0.25", {"position": v(-166, 257) * mm});
            skPoint(sketch, "E164.1.0.26", {"position": v(-194, 20) * mm});
            skPoint(sketch, "E164.1.0.27", {"position": v(-142, 62) * mm});
            skPoint(sketch, "E164.1.0.28", {"position": v(-166, 375) * mm});
            skPoint(sketch, "E164.1.0.29", {"position": v(-197, 297) * mm});
            skPoint(sketch, "E164.1.0.30", {"position": v(-163, 297) * mm});
            skPoint(sketch, "E164.1.0.31", {"position": v(-194, 40) * mm});
            skPoint(sketch, "E164.1.0.32", {"position": v(-142, 141) * mm});
            skPoint(sketch, "E164.1.0.33", {"position": v(-197, 335) * mm});
            skPoint(sketch, "E164.1.0.34", {"position": v(-166, 20) * mm});
            skPoint(sketch, "E164.1.0.35", {"position": v(-166, 277) * mm});
            skPoint(sketch, "E164.1.0.36", {"position": v(-142, 299) * mm});
            skPoint(sketch, "E164.1.0.37", {"position": v(-197, 139) * mm});
            skPoint(sketch, "E164.1.0.38", {"position": v(-166, 355) * mm});
            skPoint(sketch, "E164.1.0.39", {"position": v(-163, 139) * mm});
            skLineSegment(sketch, "E164.1.0.40", {"start": v(-222, 337) * mm, "end": v(-214, 337) * mm});
            skLineSegment(sketch, "E164.1.0.41", {"start": v(-222, 337) * mm, "end": v(-222, 329) * mm});
            skLineSegment(sketch, "E164.1.0.42", {"start": v(-222, 329) * mm, "end": v(-214, 329) * mm});
            skLineSegment(sketch, "E164.1.0.43", {"start": v(-138, 329) * mm, "end": v(-146, 329) * mm});
            skLineSegment(sketch, "E164.1.0.44", {"start": v(-162, 95) * mm, "end": v(-170, 95) * mm});
            skLineSegment(sketch, "E164.1.0.45", {"start": v(-198, 221) * mm, "end": v(-190, 221) * mm});
            skLineSegment(sketch, "E164.1.0.46", {"start": v(-222, 66) * mm, "end": v(-222, 58) * mm});
            skLineSegment(sketch, "E164.1.0.47", {"start": v(-162, 221) * mm, "end": v(-170, 221) * mm});
            skLineSegment(sketch, "E164.1.0.48", {"start": v(-222, 58) * mm, "end": v(-214, 58) * mm});
            skLineSegment(sketch, "E164.1.0.49", {"start": v(-198, 201) * mm, "end": v(-190, 201) * mm});
            skLineSegment(sketch, "E164.1.0.50", {"start": v(-222, 303) * mm, "end": v(-214, 303) * mm});
            skLineSegment(sketch, "E164.1.0.51", {"start": v(-222, 303) * mm, "end": v(-222, 295) * mm});
            skLineSegment(sketch, "E164.1.0.52", {"start": v(-222, 145) * mm, "end": v(-222, 137) * mm});
            skLineSegment(sketch, "E164.1.0.53", {"start": v(-138, 337) * mm, "end": v(-138, 329) * mm});
            skLineSegment(sketch, "E164.1.0.54", {"start": v(-222, 295) * mm, "end": v(-214, 295) * mm});
            skLineSegment(sketch, "E164.1.0.55", {"start": v(-138, 179) * mm, "end": v(-138, 171) * mm});
            skLineSegment(sketch, "E164.1.0.56", {"start": v(-138, 58) * mm, "end": v(-146, 58) * mm});
            skLineSegment(sketch, "E164.1.0.57", {"start": v(-138, 66) * mm, "end": v(-138, 58) * mm});
            skLineSegment(sketch, "E164.1.0.58", {"start": v(-146, 179) * mm, "end": v(-146, 171) * mm});
            skLineSegment(sketch, "E164.1.0.59", {"start": v(-198, 379) * mm, "end": v(-190, 379) * mm});
            skLineSegment(sketch, "E164.1.0.60", {"start": v(-201, 64) * mm, "end": v(-201, 56) * mm});
            skLineSegment(sketch, "E164.1.0.61", {"start": v(-138, 66) * mm, "end": v(-146, 66) * mm});
            skLineSegment(sketch, "E164.1.0.62", {"start": v(-198, 221) * mm, "end": v(-198, 213) * mm});
            skLineSegment(sketch, "E164.1.0.63", {"start": v(-222, 179) * mm, "end": v(-222, 171) * mm});
            skLineSegment(sketch, "E164.1.0.64", {"start": v(-222, 66) * mm, "end": v(-214, 66) * mm});
            skLineSegment(sketch, "E164.1.0.65", {"start": v(-138, 171) * mm, "end": v(-146, 171) * mm});
            skLineSegment(sketch, "E164.1.0.66", {"start": v(-222, 171) * mm, "end": v(-214, 171) * mm});
            skLineSegment(sketch, "E164.1.0.67", {"start": v(-214, 66) * mm, "end": v(-214, 58) * mm});
            skLineSegment(sketch, "E164.1.0.68", {"start": v(-190, 221) * mm, "end": v(-190, 213) * mm});
            skLineSegment(sketch, "E164.1.0.69", {"start": v(-222, 145) * mm, "end": v(-214, 145) * mm});
            skLineSegment(sketch, "E164.1.0.70", {"start": v(-193, 64) * mm, "end": v(-193, 56) * mm});
            skLineSegment(sketch, "E164.1.0.71", {"start": v(-162, 379) * mm, "end": v(-170, 379) * mm});
            skLineSegment(sketch, "E164.1.0.72", {"start": v(-162, 253) * mm, "end": v(-170, 253) * mm});
            skLineSegment(sketch, "E164.1.0.73", {"start": v(-162, 359) * mm, "end": v(-170, 359) * mm});
            skLineSegment(sketch, "E164.1.0.74", {"start": v(-162, 201) * mm, "end": v(-162, 193) * mm});
            skLineSegment(sketch, "E164.1.0.75", {"start": v(-198, 201) * mm, "end": v(-198, 193) * mm});
            skLineSegment(sketch, "E164.1.0.76", {"start": v(-162, 221) * mm, "end": v(-162, 213) * mm});
            skLineSegment(sketch, "E164.1.0.77", {"start": v(-159, 173) * mm, "end": v(-167, 173) * mm});
            skLineSegment(sketch, "E164.1.0.78", {"start": v(-190, 201) * mm, "end": v(-190, 193) * mm});
            skLineSegment(sketch, "E164.1.0.79", {"start": v(-193, 301) * mm, "end": v(-193, 293) * mm});
            skLineSegment(sketch, "E164.1.0.80", {"start": v(-198, 253) * mm, "end": v(-190, 253) * mm});
            skLineSegment(sketch, "E164.1.0.81", {"start": v(-159, 56) * mm, "end": v(-167, 56) * mm});
            skLineSegment(sketch, "E164.1.0.82", {"start": v(-201, 143) * mm, "end": v(-193, 143) * mm});
            skLineSegment(sketch, "E164.1.0.83", {"start": v(-201, 173) * mm, "end": v(-193, 173) * mm});
            skLineSegment(sketch, "E164.1.0.84", {"start": v(-198, 36) * mm, "end": v(-190, 36) * mm});
            skLineSegment(sketch, "E164.1.0.85", {"start": v(-193, 181) * mm, "end": v(-193, 173) * mm});
            skLineSegment(sketch, "E164.1.0.86", {"start": v(-162, 24) * mm, "end": v(-170, 24) * mm});
            skLineSegment(sketch, "E164.1.0.87", {"start": v(-198, 123) * mm, "end": v(-190, 123) * mm});
            skLineSegment(sketch, "E164.1.0.88", {"start": v(-201, 181) * mm, "end": v(-193, 181) * mm});
            skLineSegment(sketch, "E164.1.0.89", {"start": v(-159, 181) * mm, "end": v(-159, 173) * mm});
            skLineSegment(sketch, "E164.1.0.90", {"start": v(-198, 193) * mm, "end": v(-190, 193) * mm});
            skLineSegment(sketch, "E164.1.0.91", {"start": v(-167, 181) * mm, "end": v(-167, 173) * mm});
            skLineSegment(sketch, "E164.1.0.92", {"start": v(-198, 123) * mm, "end": v(-198, 115) * mm});
            skLineSegment(sketch, "E164.1.0.93", {"start": v(-201, 143) * mm, "end": v(-201, 135) * mm});
            skLineSegment(sketch, "E164.1.0.94", {"start": v(-159, 64) * mm, "end": v(-159, 56) * mm});
            skLineSegment(sketch, "E164.1.0.95", {"start": v(-138, 337) * mm, "end": v(-146, 337) * mm});
            skLineSegment(sketch, "E164.1.0.96", {"start": v(-198, 44) * mm, "end": v(-190, 44) * mm});
            skLineSegment(sketch, "E164.1.0.97", {"start": v(-170, 379) * mm, "end": v(-170, 371) * mm});
            skLineSegment(sketch, "E164.1.0.98", {"start": v(-190, 24) * mm, "end": v(-190, 16) * mm});
            skLineSegment(sketch, "E164.1.0.99", {"start": v(-159, 181) * mm, "end": v(-167, 181) * mm});
            skLineSegment(sketch, "E164.1.0.100", {"start": v(-198, 359) * mm, "end": v(-190, 359) * mm});
            skLineSegment(sketch, "E164.1.0.101", {"start": v(-214, 179) * mm, "end": v(-214, 171) * mm});
            skLineSegment(sketch, "E164.1.0.102", {"start": v(-201, 64) * mm, "end": v(-193, 64) * mm});
            skLineSegment(sketch, "E164.1.0.103", {"start": v(-201, 181) * mm, "end": v(-201, 173) * mm});
            skLineSegment(sketch, "E164.1.0.104", {"start": v(-222, 179) * mm, "end": v(-214, 179) * mm});
            skLineSegment(sketch, "E164.1.0.105", {"start": v(-162, 201) * mm, "end": v(-170, 201) * mm});
            skLineSegment(sketch, "E164.1.0.106", {"start": v(-198, 24) * mm, "end": v(-198, 16) * mm});
            skLineSegment(sketch, "E164.1.0.107", {"start": v(-162, 24) * mm, "end": v(-162, 16) * mm});
            skLineSegment(sketch, "E164.1.0.108", {"start": v(-198, 213) * mm, "end": v(-190, 213) * mm});
            skLineSegment(sketch, "E164.1.0.109", {"start": v(-198, 24) * mm, "end": v(-190, 24) * mm});
            skLineSegment(sketch, "E164.1.0.110", {"start": v(-162, 103) * mm, "end": v(-162, 95) * mm});
            skLineSegment(sketch, "E164.1.0.111", {"start": v(-170, 44) * mm, "end": v(-170, 36) * mm});
            skLineSegment(sketch, "E164.1.0.112", {"start": v(-162, 261) * mm, "end": v(-162, 253) * mm});
            skLineSegment(sketch, "E164.1.0.113", {"start": v(-162, 379) * mm, "end": v(-162, 371) * mm});
            skLineSegment(sketch, "E164.1.0.114", {"start": v(-138, 179) * mm, "end": v(-146, 179) * mm});
            skLineSegment(sketch, "E164.1.0.115", {"start": v(-198, 44) * mm, "end": v(-198, 36) * mm});
            skLineSegment(sketch, "E164.1.0.116", {"start": v(-190, 44) * mm, "end": v(-190, 36) * mm});
            skLineSegment(sketch, "E164.1.0.117", {"start": v(-170, 261) * mm, "end": v(-170, 253) * mm});
            skLineSegment(sketch, "E164.1.0.118", {"start": v(-167, 64) * mm, "end": v(-167, 56) * mm});
            skLineSegment(sketch, "E164.1.0.119", {"start": v(-214, 303) * mm, "end": v(-214, 295) * mm});
            skLineSegment(sketch, "E164.1.0.120", {"start": v(-201, 135) * mm, "end": v(-193, 135) * mm});
            skLineSegment(sketch, "E164.1.0.121", {"start": v(-162, 193) * mm, "end": v(-170, 193) * mm});
            skLineSegment(sketch, "E164.1.0.122", {"start": v(-201, 301) * mm, "end": v(-201, 293) * mm});
            skLineSegment(sketch, "E164.1.0.123", {"start": v(-201, 56) * mm, "end": v(-193, 56) * mm});
            skLineSegment(sketch, "E164.1.0.124", {"start": v(-198, 371) * mm, "end": v(-190, 371) * mm});
            skLineSegment(sketch, "E164.1.0.125", {"start": v(-159, 64) * mm, "end": v(-167, 64) * mm});
            skLineSegment(sketch, "E164.1.0.126", {"start": v(-198, 379) * mm, "end": v(-198, 371) * mm});
            skLineSegment(sketch, "E164.1.0.127", {"start": v(-201, 301) * mm, "end": v(-193, 301) * mm});
            skLineSegment(sketch, "E164.1.0.128", {"start": v(-162, 44) * mm, "end": v(-162, 36) * mm});
            skLineSegment(sketch, "E164.1.0.129", {"start": v(-193, 143) * mm, "end": v(-193, 135) * mm});
            skLineSegment(sketch, "E164.1.0.130", {"start": v(-222, 137) * mm, "end": v(-214, 137) * mm});
            skLineSegment(sketch, "E164.1.0.131", {"start": v(-170, 103) * mm, "end": v(-170, 95) * mm});
            skLineSegment(sketch, "E164.1.0.132", {"start": v(-170, 24) * mm, "end": v(-170, 16) * mm});
            skLineSegment(sketch, "E164.1.0.133", {"start": v(-214, 145) * mm, "end": v(-214, 137) * mm});
            skLineSegment(sketch, "E164.1.0.134", {"start": v(-190, 379) * mm, "end": v(-190, 371) * mm});
            skLineSegment(sketch, "E164.1.0.135", {"start": v(-170, 221) * mm, "end": v(-170, 213) * mm});
            skLineSegment(sketch, "E164.1.0.136", {"start": v(-146, 66) * mm, "end": v(-146, 58) * mm});
            skLineSegment(sketch, "E164.1.0.137", {"start": v(-198, 351) * mm, "end": v(-190, 351) * mm});
            skLineSegment(sketch, "E164.1.0.138", {"start": v(-170, 359) * mm, "end": v(-170, 351) * mm});
            skLineSegment(sketch, "E164.1.0.139", {"start": v(-190, 103) * mm, "end": v(-190, 95) * mm});
            skLineSegment(sketch, "E164.1.0.140", {"start": v(-198, 115) * mm, "end": v(-190, 115) * mm});
            skLineSegment(sketch, "E164.1.0.141", {"start": v(-162, 371) * mm, "end": v(-170, 371) * mm});
            skLineSegment(sketch, "E164.1.0.142", {"start": v(-162, 36) * mm, "end": v(-170, 36) * mm});
            skLineSegment(sketch, "E164.1.0.143", {"start": v(-201, 331) * mm, "end": v(-193, 331) * mm});
            skLineSegment(sketch, "E164.1.0.144", {"start": v(-159, 143) * mm, "end": v(-159, 135) * mm});
            skLineSegment(sketch, "E164.1.0.145", {"start": v(-159, 331) * mm, "end": v(-167, 331) * mm});
            skLineSegment(sketch, "E164.1.0.146", {"start": v(-138, 145) * mm, "end": v(-138, 137) * mm});
            skLineSegment(sketch, "E164.1.0.147", {"start": v(-190, 261) * mm, "end": v(-190, 253) * mm});
            skLineSegment(sketch, "E164.1.0.148", {"start": v(-167, 339) * mm, "end": v(-167, 331) * mm});
            skLineSegment(sketch, "E164.1.0.149", {"start": v(-198, 261) * mm, "end": v(-198, 253) * mm});
            skLineSegment(sketch, "E164.1.0.150", {"start": v(-198, 359) * mm, "end": v(-198, 351) * mm});
            skLineSegment(sketch, "E164.1.0.151", {"start": v(-159, 135) * mm, "end": v(-167, 135) * mm});
            skLineSegment(sketch, "E164.1.0.152", {"start": v(-167, 301) * mm, "end": v(-167, 293) * mm});
            skLineSegment(sketch, "E164.1.0.153", {"start": v(-146, 337) * mm, "end": v(-146, 329) * mm});
            skLineSegment(sketch, "E164.1.0.154", {"start": v(-201, 293) * mm, "end": v(-193, 293) * mm});
            skLineSegment(sketch, "E164.1.0.155", {"start": v(-214, 337) * mm, "end": v(-214, 329) * mm});
            skLineSegment(sketch, "E164.1.0.156", {"start": v(-198, 103) * mm, "end": v(-198, 95) * mm});
            skLineSegment(sketch, "E164.1.0.157", {"start": v(-193, 339) * mm, "end": v(-193, 331) * mm});
            skLineSegment(sketch, "E164.1.0.158", {"start": v(-159, 293) * mm, "end": v(-167, 293) * mm});
            skLineSegment(sketch, "E164.1.0.159", {"start": v(-162, 103) * mm, "end": v(-170, 103) * mm});
            skLineSegment(sketch, "E164.1.0.160", {"start": v(-162, 16) * mm, "end": v(-170, 16) * mm});
            skLineSegment(sketch, "E164.1.0.161", {"start": v(-162, 359) * mm, "end": v(-162, 351) * mm});
            skLineSegment(sketch, "E164.1.0.162", {"start": v(-198, 95) * mm, "end": v(-190, 95) * mm});
            skLineSegment(sketch, "E164.1.0.163", {"start": v(-146, 303) * mm, "end": v(-146, 295) * mm});
            skLineSegment(sketch, "E164.1.0.164", {"start": v(-162, 123) * mm, "end": v(-162, 115) * mm});
            skLineSegment(sketch, "E164.1.0.165", {"start": v(-146, 145) * mm, "end": v(-146, 137) * mm});
            skLineSegment(sketch, "E164.1.0.166", {"start": v(-162, 115) * mm, "end": v(-170, 115) * mm});
            skLineSegment(sketch, "E164.1.0.167", {"start": v(-198, 16) * mm, "end": v(-190, 16) * mm});
            skLineSegment(sketch, "E164.1.0.168", {"start": v(-162, 281) * mm, "end": v(-162, 273) * mm});
            skLineSegment(sketch, "E164.1.0.169", {"start": v(-138, 303) * mm, "end": v(-138, 295) * mm});
            skLineSegment(sketch, "E164.1.0.170", {"start": v(-190, 123) * mm, "end": v(-190, 115) * mm});
            skLineSegment(sketch, "E164.1.0.171", {"start": v(-159, 339) * mm, "end": v(-167, 339) * mm});
            skLineSegment(sketch, "E164.1.0.172", {"start": v(-162, 123) * mm, "end": v(-170, 123) * mm});
            skLineSegment(sketch, "E164.1.0.173", {"start": v(-162, 273) * mm, "end": v(-170, 273) * mm});
            skLineSegment(sketch, "E164.1.0.174", {"start": v(-198, 281) * mm, "end": v(-198, 273) * mm});
            skLineSegment(sketch, "E164.1.0.175", {"start": v(-162, 261) * mm, "end": v(-170, 261) * mm});
            skLineSegment(sketch, "E164.1.0.176", {"start": v(-190, 359) * mm, "end": v(-190, 351) * mm});
            skLineSegment(sketch, "E164.1.0.177", {"start": v(-159, 143) * mm, "end": v(-167, 143) * mm});
            skLineSegment(sketch, "E164.1.0.178", {"start": v(-170, 201) * mm, "end": v(-170, 193) * mm});
            skLineSegment(sketch, "E164.1.0.179", {"start": v(-167, 143) * mm, "end": v(-167, 135) * mm});
            skLineSegment(sketch, "E164.1.0.180", {"start": v(-159, 301) * mm, "end": v(-159, 293) * mm});
            skLineSegment(sketch, "E164.1.0.181", {"start": v(-138, 145) * mm, "end": v(-146, 145) * mm});
            skLineSegment(sketch, "E164.1.0.182", {"start": v(-159, 301) * mm, "end": v(-167, 301) * mm});
            skLineSegment(sketch, "E164.1.0.183", {"start": v(-198, 273) * mm, "end": v(-190, 273) * mm});
            skLineSegment(sketch, "E164.1.0.184", {"start": v(-198, 261) * mm, "end": v(-190, 261) * mm});
            skLineSegment(sketch, "E164.1.0.185", {"start": v(-198, 281) * mm, "end": v(-190, 281) * mm});
            skLineSegment(sketch, "E164.1.0.186", {"start": v(-138, 303) * mm, "end": v(-146, 303) * mm});
            skLineSegment(sketch, "E164.1.0.187", {"start": v(-162, 281) * mm, "end": v(-170, 281) * mm});
            skLineSegment(sketch, "E164.1.0.188", {"start": v(-201, 339) * mm, "end": v(-201, 331) * mm});
            skLineSegment(sketch, "E164.1.0.189", {"start": v(-162, 351) * mm, "end": v(-170, 351) * mm});
            skLineSegment(sketch, "E164.1.0.190", {"start": v(-162, 213) * mm, "end": v(-170, 213) * mm});
            skLineSegment(sketch, "E164.1.0.191", {"start": v(-162, 44) * mm, "end": v(-170, 44) * mm});
            skLineSegment(sketch, "E164.1.0.192", {"start": v(-170, 281) * mm, "end": v(-170, 273) * mm});
            skLineSegment(sketch, "E164.1.0.193", {"start": v(-170, 123) * mm, "end": v(-170, 115) * mm});
            skLineSegment(sketch, "E164.1.0.194", {"start": v(-201, 339) * mm, "end": v(-193, 339) * mm});
            skLineSegment(sketch, "E164.1.0.195", {"start": v(-138, 137) * mm, "end": v(-146, 137) * mm});
            skLineSegment(sketch, "E164.1.0.196", {"start": v(-138, 295) * mm, "end": v(-146, 295) * mm});
            skLineSegment(sketch, "E164.1.0.197", {"start": v(-159, 339) * mm, "end": v(-159, 331) * mm});
            skLineSegment(sketch, "E164.1.0.198", {"start": v(-198, 103) * mm, "end": v(-190, 103) * mm});
            skLineSegment(sketch, "E164.1.0.199", {"start": v(-190, 281) * mm, "end": v(-190, 273) * mm});
            skPoint(sketch, "E164.2.0.0", {"position": v(-286, 197) * mm});
            skPoint(sketch, "E164.2.0.1", {"position": v(-314, 119) * mm});
            skPoint(sketch, "E164.2.0.2", {"position": v(-286, 119) * mm});
            skPoint(sketch, "E164.2.0.3", {"position": v(-262, 175) * mm});
            skPoint(sketch, "E164.2.0.4", {"position": v(-338, 299) * mm});
            skPoint(sketch, "E164.2.0.5", {"position": v(-338, 141) * mm});
            skPoint(sketch, "E164.2.0.6", {"position": v(-314, 217) * mm});
            skPoint(sketch, "E164.2.0.7", {"position": v(-314, 375) * mm});
            skPoint(sketch, "E164.2.0.8", {"position": v(-317, 60) * mm});
            skPoint(sketch, "E164.2.0.9", {"position": v(-338, 333) * mm});
            skPoint(sketch, "E164.2.0.10", {"position": v(-283, 335) * mm});
            skPoint(sketch, "E164.2.0.11", {"position": v(-314, 99) * mm});
            skPoint(sketch, "E164.2.0.12", {"position": v(-262, 333) * mm});
            skPoint(sketch, "E164.2.0.13", {"position": v(-314, 277) * mm});
            skPoint(sketch, "E164.2.0.14", {"position": v(-286, 217) * mm});
            skPoint(sketch, "E164.2.0.15", {"position": v(-314, 257) * mm});
            skPoint(sketch, "E164.2.0.16", {"position": v(-338, 175) * mm});
            skPoint(sketch, "E164.2.0.17", {"position": v(-286, 40) * mm});
            skPoint(sketch, "E164.2.0.18", {"position": v(-283, 60) * mm});
            skPoint(sketch, "E164.2.0.19", {"position": v(-338, 62) * mm});
            skPoint(sketch, "E164.2.0.20", {"position": v(-283, 177) * mm});
            skPoint(sketch, "E164.2.0.21", {"position": v(-286, 99) * mm});
            skPoint(sketch, "E164.2.0.22", {"position": v(-317, 177) * mm});
            skPoint(sketch, "E164.2.0.23", {"position": v(-314, 355) * mm});
            skPoint(sketch, "E164.2.0.24", {"position": v(-314, 197) * mm});
            skPoint(sketch, "E164.2.0.25", {"position": v(-286, 257) * mm});
            skPoint(sketch, "E164.2.0.26", {"position": v(-314, 20) * mm});
            skPoint(sketch, "E164.2.0.27", {"position": v(-262, 62) * mm});
            skPoint(sketch, "E164.2.0.28", {"position": v(-286, 375) * mm});
            skPoint(sketch, "E164.2.0.29", {"position": v(-317, 297) * mm});
            skPoint(sketch, "E164.2.0.30", {"position": v(-283, 297) * mm});
            skPoint(sketch, "E164.2.0.31", {"position": v(-314, 40) * mm});
            skPoint(sketch, "E164.2.0.32", {"position": v(-262, 141) * mm});
            skPoint(sketch, "E164.2.0.33", {"position": v(-317, 335) * mm});
            skPoint(sketch, "E164.2.0.34", {"position": v(-286, 20) * mm});
            skPoint(sketch, "E164.2.0.35", {"position": v(-286, 277) * mm});
            skPoint(sketch, "E164.2.0.36", {"position": v(-262, 299) * mm});
            skPoint(sketch, "E164.2.0.37", {"position": v(-317, 139) * mm});
            skPoint(sketch, "E164.2.0.38", {"position": v(-286, 355) * mm});
            skPoint(sketch, "E164.2.0.39", {"position": v(-283, 139) * mm});
            skLineSegment(sketch, "E164.2.0.40", {"start": v(-342, 337) * mm, "end": v(-334, 337) * mm});
            skLineSegment(sketch, "E164.2.0.41", {"start": v(-342, 337) * mm, "end": v(-342, 329) * mm});
            skLineSegment(sketch, "E164.2.0.42", {"start": v(-342, 329) * mm, "end": v(-334, 329) * mm});
            skLineSegment(sketch, "E164.2.0.43", {"start": v(-258, 329) * mm, "end": v(-266, 329) * mm});
            skLineSegment(sketch, "E164.2.0.44", {"start": v(-282, 95) * mm, "end": v(-290, 95) * mm});
            skLineSegment(sketch, "E164.2.0.45", {"start": v(-318, 221) * mm, "end": v(-310, 221) * mm});
            skLineSegment(sketch, "E164.2.0.46", {"start": v(-342, 66) * mm, "end": v(-342, 58) * mm});
            skLineSegment(sketch, "E164.2.0.47", {"start": v(-282, 221) * mm, "end": v(-290, 221) * mm});
            skLineSegment(sketch, "E164.2.0.48", {"start": v(-342, 58) * mm, "end": v(-334, 58) * mm});
            skLineSegment(sketch, "E164.2.0.49", {"start": v(-318, 201) * mm, "end": v(-310, 201) * mm});
            skLineSegment(sketch, "E164.2.0.50", {"start": v(-342, 303) * mm, "end": v(-334, 303) * mm});
            skLineSegment(sketch, "E164.2.0.51", {"start": v(-342, 303) * mm, "end": v(-342, 295) * mm});
            skLineSegment(sketch, "E164.2.0.52", {"start": v(-342, 145) * mm, "end": v(-342, 137) * mm});
            skLineSegment(sketch, "E164.2.0.53", {"start": v(-258, 337) * mm, "end": v(-258, 329) * mm});
            skLineSegment(sketch, "E164.2.0.54", {"start": v(-342, 295) * mm, "end": v(-334, 295) * mm});
            skLineSegment(sketch, "E164.2.0.55", {"start": v(-258, 179) * mm, "end": v(-258, 171) * mm});
            skLineSegment(sketch, "E164.2.0.56", {"start": v(-258, 58) * mm, "end": v(-266, 58) * mm});
            skLineSegment(sketch, "E164.2.0.57", {"start": v(-258, 66) * mm, "end": v(-258, 58) * mm});
            skLineSegment(sketch, "E164.2.0.58", {"start": v(-266, 179) * mm, "end": v(-266, 171) * mm});
            skLineSegment(sketch, "E164.2.0.59", {"start": v(-318, 379) * mm, "end": v(-310, 379) * mm});
            skLineSegment(sketch, "E164.2.0.60", {"start": v(-321, 64) * mm, "end": v(-321, 56) * mm});
            skLineSegment(sketch, "E164.2.0.61", {"start": v(-258, 66) * mm, "end": v(-266, 66) * mm});
            skLineSegment(sketch, "E164.2.0.62", {"start": v(-318, 221) * mm, "end": v(-318, 213) * mm});
            skLineSegment(sketch, "E164.2.0.63", {"start": v(-342, 179) * mm, "end": v(-342, 171) * mm});
            skLineSegment(sketch, "E164.2.0.64", {"start": v(-342, 66) * mm, "end": v(-334, 66) * mm});
            skLineSegment(sketch, "E164.2.0.65", {"start": v(-258, 171) * mm, "end": v(-266, 171) * mm});
            skLineSegment(sketch, "E164.2.0.66", {"start": v(-342, 171) * mm, "end": v(-334, 171) * mm});
            skLineSegment(sketch, "E164.2.0.67", {"start": v(-334, 66) * mm, "end": v(-334, 58) * mm});
            skLineSegment(sketch, "E164.2.0.68", {"start": v(-310, 221) * mm, "end": v(-310, 213) * mm});
            skLineSegment(sketch, "E164.2.0.69", {"start": v(-342, 145) * mm, "end": v(-334, 145) * mm});
            skLineSegment(sketch, "E164.2.0.70", {"start": v(-313, 64) * mm, "end": v(-313, 56) * mm});
            skLineSegment(sketch, "E164.2.0.71", {"start": v(-282, 379) * mm, "end": v(-290, 379) * mm});
            skLineSegment(sketch, "E164.2.0.72", {"start": v(-282, 253) * mm, "end": v(-290, 253) * mm});
            skLineSegment(sketch, "E164.2.0.73", {"start": v(-282, 359) * mm, "end": v(-290, 359) * mm});
            skLineSegment(sketch, "E164.2.0.74", {"start": v(-282, 201) * mm, "end": v(-282, 193) * mm});
            skLineSegment(sketch, "E164.2.0.75", {"start": v(-318, 201) * mm, "end": v(-318, 193) * mm});
            skLineSegment(sketch, "E164.2.0.76", {"start": v(-282, 221) * mm, "end": v(-282, 213) * mm});
            skLineSegment(sketch, "E164.2.0.77", {"start": v(-279, 173) * mm, "end": v(-287, 173) * mm});
            skLineSegment(sketch, "E164.2.0.78", {"start": v(-310, 201) * mm, "end": v(-310, 193) * mm});
            skLineSegment(sketch, "E164.2.0.79", {"start": v(-313, 301) * mm, "end": v(-313, 293) * mm});
            skLineSegment(sketch, "E164.2.0.80", {"start": v(-318, 253) * mm, "end": v(-310, 253) * mm});
            skLineSegment(sketch, "E164.2.0.81", {"start": v(-279, 56) * mm, "end": v(-287, 56) * mm});
            skLineSegment(sketch, "E164.2.0.82", {"start": v(-321, 143) * mm, "end": v(-313, 143) * mm});
            skLineSegment(sketch, "E164.2.0.83", {"start": v(-321, 173) * mm, "end": v(-313, 173) * mm});
            skLineSegment(sketch, "E164.2.0.84", {"start": v(-318, 36) * mm, "end": v(-310, 36) * mm});
            skLineSegment(sketch, "E164.2.0.85", {"start": v(-313, 181) * mm, "end": v(-313, 173) * mm});
            skLineSegment(sketch, "E164.2.0.86", {"start": v(-282, 24) * mm, "end": v(-290, 24) * mm});
            skLineSegment(sketch, "E164.2.0.87", {"start": v(-318, 123) * mm, "end": v(-310, 123) * mm});
            skLineSegment(sketch, "E164.2.0.88", {"start": v(-321, 181) * mm, "end": v(-313, 181) * mm});
            skLineSegment(sketch, "E164.2.0.89", {"start": v(-279, 181) * mm, "end": v(-279, 173) * mm});
            skLineSegment(sketch, "E164.2.0.90", {"start": v(-318, 193) * mm, "end": v(-310, 193) * mm});
            skLineSegment(sketch, "E164.2.0.91", {"start": v(-287, 181) * mm, "end": v(-287, 173) * mm});
            skLineSegment(sketch, "E164.2.0.92", {"start": v(-318, 123) * mm, "end": v(-318, 115) * mm});
            skLineSegment(sketch, "E164.2.0.93", {"start": v(-321, 143) * mm, "end": v(-321, 135) * mm});
            skLineSegment(sketch, "E164.2.0.94", {"start": v(-279, 64) * mm, "end": v(-279, 56) * mm});
            skLineSegment(sketch, "E164.2.0.95", {"start": v(-258, 337) * mm, "end": v(-266, 337) * mm});
            skLineSegment(sketch, "E164.2.0.96", {"start": v(-318, 44) * mm, "end": v(-310, 44) * mm});
            skLineSegment(sketch, "E164.2.0.97", {"start": v(-290, 379) * mm, "end": v(-290, 371) * mm});
            skLineSegment(sketch, "E164.2.0.98", {"start": v(-310, 24) * mm, "end": v(-310, 16) * mm});
            skLineSegment(sketch, "E164.2.0.99", {"start": v(-279, 181) * mm, "end": v(-287, 181) * mm});
            skLineSegment(sketch, "E164.2.0.100", {"start": v(-318, 359) * mm, "end": v(-310, 359) * mm});
            skLineSegment(sketch, "E164.2.0.101", {"start": v(-334, 179) * mm, "end": v(-334, 171) * mm});
            skLineSegment(sketch, "E164.2.0.102", {"start": v(-321, 64) * mm, "end": v(-313, 64) * mm});
            skLineSegment(sketch, "E164.2.0.103", {"start": v(-321, 181) * mm, "end": v(-321, 173) * mm});
            skLineSegment(sketch, "E164.2.0.104", {"start": v(-342, 179) * mm, "end": v(-334, 179) * mm});
            skLineSegment(sketch, "E164.2.0.105", {"start": v(-282, 201) * mm, "end": v(-290, 201) * mm});
            skLineSegment(sketch, "E164.2.0.106", {"start": v(-318, 24) * mm, "end": v(-318, 16) * mm});
            skLineSegment(sketch, "E164.2.0.107", {"start": v(-282, 24) * mm, "end": v(-282, 16) * mm});
            skLineSegment(sketch, "E164.2.0.108", {"start": v(-318, 213) * mm, "end": v(-310, 213) * mm});
            skLineSegment(sketch, "E164.2.0.109", {"start": v(-318, 24) * mm, "end": v(-310, 24) * mm});
            skLineSegment(sketch, "E164.2.0.110", {"start": v(-282, 103) * mm, "end": v(-282, 95) * mm});
            skLineSegment(sketch, "E164.2.0.111", {"start": v(-290, 44) * mm, "end": v(-290, 36) * mm});
            skLineSegment(sketch, "E164.2.0.112", {"start": v(-282, 261) * mm, "end": v(-282, 253) * mm});
            skLineSegment(sketch, "E164.2.0.113", {"start": v(-282, 379) * mm, "end": v(-282, 371) * mm});
            skLineSegment(sketch, "E164.2.0.114", {"start": v(-258, 179) * mm, "end": v(-266, 179) * mm});
            skLineSegment(sketch, "E164.2.0.115", {"start": v(-318, 44) * mm, "end": v(-318, 36) * mm});
            skLineSegment(sketch, "E164.2.0.116", {"start": v(-310, 44) * mm, "end": v(-310, 36) * mm});
            skLineSegment(sketch, "E164.2.0.117", {"start": v(-290, 261) * mm, "end": v(-290, 253) * mm});
            skLineSegment(sketch, "E164.2.0.118", {"start": v(-287, 64) * mm, "end": v(-287, 56) * mm});
            skLineSegment(sketch, "E164.2.0.119", {"start": v(-334, 303) * mm, "end": v(-334, 295) * mm});
            skLineSegment(sketch, "E164.2.0.120", {"start": v(-321, 135) * mm, "end": v(-313, 135) * mm});
            skLineSegment(sketch, "E164.2.0.121", {"start": v(-282, 193) * mm, "end": v(-290, 193) * mm});
            skLineSegment(sketch, "E164.2.0.122", {"start": v(-321, 301) * mm, "end": v(-321, 293) * mm});
            skLineSegment(sketch, "E164.2.0.123", {"start": v(-321, 56) * mm, "end": v(-313, 56) * mm});
            skLineSegment(sketch, "E164.2.0.124", {"start": v(-318, 371) * mm, "end": v(-310, 371) * mm});
            skLineSegment(sketch, "E164.2.0.125", {"start": v(-279, 64) * mm, "end": v(-287, 64) * mm});
            skLineSegment(sketch, "E164.2.0.126", {"start": v(-318, 379) * mm, "end": v(-318, 371) * mm});
            skLineSegment(sketch, "E164.2.0.127", {"start": v(-321, 301) * mm, "end": v(-313, 301) * mm});
            skLineSegment(sketch, "E164.2.0.128", {"start": v(-282, 44) * mm, "end": v(-282, 36) * mm});
            skLineSegment(sketch, "E164.2.0.129", {"start": v(-313, 143) * mm, "end": v(-313, 135) * mm});
            skLineSegment(sketch, "E164.2.0.130", {"start": v(-342, 137) * mm, "end": v(-334, 137) * mm});
            skLineSegment(sketch, "E164.2.0.131", {"start": v(-290, 103) * mm, "end": v(-290, 95) * mm});
            skLineSegment(sketch, "E164.2.0.132", {"start": v(-290, 24) * mm, "end": v(-290, 16) * mm});
            skLineSegment(sketch, "E164.2.0.133", {"start": v(-334, 145) * mm, "end": v(-334, 137) * mm});
            skLineSegment(sketch, "E164.2.0.134", {"start": v(-310, 379) * mm, "end": v(-310, 371) * mm});
            skLineSegment(sketch, "E164.2.0.135", {"start": v(-290, 221) * mm, "end": v(-290, 213) * mm});
            skLineSegment(sketch, "E164.2.0.136", {"start": v(-266, 66) * mm, "end": v(-266, 58) * mm});
            skLineSegment(sketch, "E164.2.0.137", {"start": v(-318, 351) * mm, "end": v(-310, 351) * mm});
            skLineSegment(sketch, "E164.2.0.138", {"start": v(-290, 359) * mm, "end": v(-290, 351) * mm});
            skLineSegment(sketch, "E164.2.0.139", {"start": v(-310, 103) * mm, "end": v(-310, 95) * mm});
            skLineSegment(sketch, "E164.2.0.140", {"start": v(-318, 115) * mm, "end": v(-310, 115) * mm});
            skLineSegment(sketch, "E164.2.0.141", {"start": v(-282, 371) * mm, "end": v(-290, 371) * mm});
            skLineSegment(sketch, "E164.2.0.142", {"start": v(-282, 36) * mm, "end": v(-290, 36) * mm});
            skLineSegment(sketch, "E164.2.0.143", {"start": v(-321, 331) * mm, "end": v(-313, 331) * mm});
            skLineSegment(sketch, "E164.2.0.144", {"start": v(-279, 143) * mm, "end": v(-279, 135) * mm});
            skLineSegment(sketch, "E164.2.0.145", {"start": v(-279, 331) * mm, "end": v(-287, 331) * mm});
            skLineSegment(sketch, "E164.2.0.146", {"start": v(-258, 145) * mm, "end": v(-258, 137) * mm});
            skLineSegment(sketch, "E164.2.0.147", {"start": v(-310, 261) * mm, "end": v(-310, 253) * mm});
            skLineSegment(sketch, "E164.2.0.148", {"start": v(-287, 339) * mm, "end": v(-287, 331) * mm});
            skLineSegment(sketch, "E164.2.0.149", {"start": v(-318, 261) * mm, "end": v(-318, 253) * mm});
            skLineSegment(sketch, "E164.2.0.150", {"start": v(-318, 359) * mm, "end": v(-318, 351) * mm});
            skLineSegment(sketch, "E164.2.0.151", {"start": v(-279, 135) * mm, "end": v(-287, 135) * mm});
            skLineSegment(sketch, "E164.2.0.152", {"start": v(-287, 301) * mm, "end": v(-287, 293) * mm});
            skLineSegment(sketch, "E164.2.0.153", {"start": v(-266, 337) * mm, "end": v(-266, 329) * mm});
            skLineSegment(sketch, "E164.2.0.154", {"start": v(-321, 293) * mm, "end": v(-313, 293) * mm});
            skLineSegment(sketch, "E164.2.0.155", {"start": v(-334, 337) * mm, "end": v(-334, 329) * mm});
            skLineSegment(sketch, "E164.2.0.156", {"start": v(-318, 103) * mm, "end": v(-318, 95) * mm});
            skLineSegment(sketch, "E164.2.0.157", {"start": v(-313, 339) * mm, "end": v(-313, 331) * mm});
            skLineSegment(sketch, "E164.2.0.158", {"start": v(-279, 293) * mm, "end": v(-287, 293) * mm});
            skLineSegment(sketch, "E164.2.0.159", {"start": v(-282, 103) * mm, "end": v(-290, 103) * mm});
            skLineSegment(sketch, "E164.2.0.160", {"start": v(-282, 16) * mm, "end": v(-290, 16) * mm});
            skLineSegment(sketch, "E164.2.0.161", {"start": v(-282, 359) * mm, "end": v(-282, 351) * mm});
            skLineSegment(sketch, "E164.2.0.162", {"start": v(-318, 95) * mm, "end": v(-310, 95) * mm});
            skLineSegment(sketch, "E164.2.0.163", {"start": v(-266, 303) * mm, "end": v(-266, 295) * mm});
            skLineSegment(sketch, "E164.2.0.164", {"start": v(-282, 123) * mm, "end": v(-282, 115) * mm});
            skLineSegment(sketch, "E164.2.0.165", {"start": v(-266, 145) * mm, "end": v(-266, 137) * mm});
            skLineSegment(sketch, "E164.2.0.166", {"start": v(-282, 115) * mm, "end": v(-290, 115) * mm});
            skLineSegment(sketch, "E164.2.0.167", {"start": v(-318, 16) * mm, "end": v(-310, 16) * mm});
            skLineSegment(sketch, "E164.2.0.168", {"start": v(-282, 281) * mm, "end": v(-282, 273) * mm});
            skLineSegment(sketch, "E164.2.0.169", {"start": v(-258, 303) * mm, "end": v(-258, 295) * mm});
            skLineSegment(sketch, "E164.2.0.170", {"start": v(-310, 123) * mm, "end": v(-310, 115) * mm});
            skLineSegment(sketch, "E164.2.0.171", {"start": v(-279, 339) * mm, "end": v(-287, 339) * mm});
            skLineSegment(sketch, "E164.2.0.172", {"start": v(-282, 123) * mm, "end": v(-290, 123) * mm});
            skLineSegment(sketch, "E164.2.0.173", {"start": v(-282, 273) * mm, "end": v(-290, 273) * mm});
            skLineSegment(sketch, "E164.2.0.174", {"start": v(-318, 281) * mm, "end": v(-318, 273) * mm});
            skLineSegment(sketch, "E164.2.0.175", {"start": v(-282, 261) * mm, "end": v(-290, 261) * mm});
            skLineSegment(sketch, "E164.2.0.176", {"start": v(-310, 359) * mm, "end": v(-310, 351) * mm});
            skLineSegment(sketch, "E164.2.0.177", {"start": v(-279, 143) * mm, "end": v(-287, 143) * mm});
            skLineSegment(sketch, "E164.2.0.178", {"start": v(-290, 201) * mm, "end": v(-290, 193) * mm});
            skLineSegment(sketch, "E164.2.0.179", {"start": v(-287, 143) * mm, "end": v(-287, 135) * mm});
            skLineSegment(sketch, "E164.2.0.180", {"start": v(-279, 301) * mm, "end": v(-279, 293) * mm});
            skLineSegment(sketch, "E164.2.0.181", {"start": v(-258, 145) * mm, "end": v(-266, 145) * mm});
            skLineSegment(sketch, "E164.2.0.182", {"start": v(-279, 301) * mm, "end": v(-287, 301) * mm});
            skLineSegment(sketch, "E164.2.0.183", {"start": v(-318, 273) * mm, "end": v(-310, 273) * mm});
            skLineSegment(sketch, "E164.2.0.184", {"start": v(-318, 261) * mm, "end": v(-310, 261) * mm});
            skLineSegment(sketch, "E164.2.0.185", {"start": v(-318, 281) * mm, "end": v(-310, 281) * mm});
            skLineSegment(sketch, "E164.2.0.186", {"start": v(-258, 303) * mm, "end": v(-266, 303) * mm});
            skLineSegment(sketch, "E164.2.0.187", {"start": v(-282, 281) * mm, "end": v(-290, 281) * mm});
            skLineSegment(sketch, "E164.2.0.188", {"start": v(-321, 339) * mm, "end": v(-321, 331) * mm});
            skLineSegment(sketch, "E164.2.0.189", {"start": v(-282, 351) * mm, "end": v(-290, 351) * mm});
            skLineSegment(sketch, "E164.2.0.190", {"start": v(-282, 213) * mm, "end": v(-290, 213) * mm});
            skLineSegment(sketch, "E164.2.0.191", {"start": v(-282, 44) * mm, "end": v(-290, 44) * mm});
            skLineSegment(sketch, "E164.2.0.192", {"start": v(-290, 281) * mm, "end": v(-290, 273) * mm});
            skLineSegment(sketch, "E164.2.0.193", {"start": v(-290, 123) * mm, "end": v(-290, 115) * mm});
            skLineSegment(sketch, "E164.2.0.194", {"start": v(-321, 339) * mm, "end": v(-313, 339) * mm});
            skLineSegment(sketch, "E164.2.0.195", {"start": v(-258, 137) * mm, "end": v(-266, 137) * mm});
            skLineSegment(sketch, "E164.2.0.196", {"start": v(-258, 295) * mm, "end": v(-266, 295) * mm});
            skLineSegment(sketch, "E164.2.0.197", {"start": v(-279, 339) * mm, "end": v(-279, 331) * mm});
            skLineSegment(sketch, "E164.2.0.198", {"start": v(-318, 103) * mm, "end": v(-310, 103) * mm});
            skLineSegment(sketch, "E164.2.0.199", {"start": v(-310, 281) * mm, "end": v(-310, 273) * mm});
            skPoint(sketch, "E164.3.0.0", {"position": v(-406, 197) * mm});
            skPoint(sketch, "E164.3.0.1", {"position": v(-434, 119) * mm});
            skPoint(sketch, "E164.3.0.2", {"position": v(-406, 119) * mm});
            skPoint(sketch, "E164.3.0.3", {"position": v(-382, 175) * mm});
            skPoint(sketch, "E164.3.0.4", {"position": v(-458, 299) * mm});
            skPoint(sketch, "E164.3.0.5", {"position": v(-458, 141) * mm});
            skPoint(sketch, "E164.3.0.6", {"position": v(-434, 217) * mm});
            skPoint(sketch, "E164.3.0.7", {"position": v(-434, 375) * mm});
            skPoint(sketch, "E164.3.0.8", {"position": v(-437, 60) * mm});
            skPoint(sketch, "E164.3.0.9", {"position": v(-458, 333) * mm});
            skPoint(sketch, "E164.3.0.10", {"position": v(-403, 335) * mm});
            skPoint(sketch, "E164.3.0.11", {"position": v(-434, 99) * mm});
            skPoint(sketch, "E164.3.0.12", {"position": v(-382, 333) * mm});
            skPoint(sketch, "E164.3.0.13", {"position": v(-434, 277) * mm});
            skPoint(sketch, "E164.3.0.14", {"position": v(-406, 217) * mm});
            skPoint(sketch, "E164.3.0.15", {"position": v(-434, 257) * mm});
            skPoint(sketch, "E164.3.0.16", {"position": v(-458, 175) * mm});
            skPoint(sketch, "E164.3.0.17", {"position": v(-406, 40) * mm});
            skPoint(sketch, "E164.3.0.18", {"position": v(-403, 60) * mm});
            skPoint(sketch, "E164.3.0.19", {"position": v(-458, 62) * mm});
            skPoint(sketch, "E164.3.0.20", {"position": v(-403, 177) * mm});
            skPoint(sketch, "E164.3.0.21", {"position": v(-406, 99) * mm});
            skPoint(sketch, "E164.3.0.22", {"position": v(-437, 177) * mm});
            skPoint(sketch, "E164.3.0.23", {"position": v(-434, 355) * mm});
            skPoint(sketch, "E164.3.0.24", {"position": v(-434, 197) * mm});
            skPoint(sketch, "E164.3.0.25", {"position": v(-406, 257) * mm});
            skPoint(sketch, "E164.3.0.26", {"position": v(-434, 20) * mm});
            skPoint(sketch, "E164.3.0.27", {"position": v(-382, 62) * mm});
            skPoint(sketch, "E164.3.0.28", {"position": v(-406, 375) * mm});
            skPoint(sketch, "E164.3.0.29", {"position": v(-437, 297) * mm});
            skPoint(sketch, "E164.3.0.30", {"position": v(-403, 297) * mm});
            skPoint(sketch, "E164.3.0.31", {"position": v(-434, 40) * mm});
            skPoint(sketch, "E164.3.0.32", {"position": v(-382, 141) * mm});
            skPoint(sketch, "E164.3.0.33", {"position": v(-437, 335) * mm});
            skPoint(sketch, "E164.3.0.34", {"position": v(-406, 20) * mm});
            skPoint(sketch, "E164.3.0.35", {"position": v(-406, 277) * mm});
            skPoint(sketch, "E164.3.0.36", {"position": v(-382, 299) * mm});
            skPoint(sketch, "E164.3.0.37", {"position": v(-437, 139) * mm});
            skPoint(sketch, "E164.3.0.38", {"position": v(-406, 355) * mm});
            skPoint(sketch, "E164.3.0.39", {"position": v(-403, 139) * mm});
            skLineSegment(sketch, "E164.3.0.40", {"start": v(-462, 337) * mm, "end": v(-454, 337) * mm});
            skLineSegment(sketch, "E164.3.0.41", {"start": v(-462, 337) * mm, "end": v(-462, 329) * mm});
            skLineSegment(sketch, "E164.3.0.42", {"start": v(-462, 329) * mm, "end": v(-454, 329) * mm});
            skLineSegment(sketch, "E164.3.0.43", {"start": v(-378, 329) * mm, "end": v(-386, 329) * mm});
            skLineSegment(sketch, "E164.3.0.44", {"start": v(-402, 95) * mm, "end": v(-410, 95) * mm});
            skLineSegment(sketch, "E164.3.0.45", {"start": v(-438, 221) * mm, "end": v(-430, 221) * mm});
            skLineSegment(sketch, "E164.3.0.46", {"start": v(-462, 66) * mm, "end": v(-462, 58) * mm});
            skLineSegment(sketch, "E164.3.0.47", {"start": v(-402, 221) * mm, "end": v(-410, 221) * mm});
            skLineSegment(sketch, "E164.3.0.48", {"start": v(-462, 58) * mm, "end": v(-454, 58) * mm});
            skLineSegment(sketch, "E164.3.0.49", {"start": v(-438, 201) * mm, "end": v(-430, 201) * mm});
            skLineSegment(sketch, "E164.3.0.50", {"start": v(-462, 303) * mm, "end": v(-454, 303) * mm});
            skLineSegment(sketch, "E164.3.0.51", {"start": v(-462, 303) * mm, "end": v(-462, 295) * mm});
            skLineSegment(sketch, "E164.3.0.52", {"start": v(-462, 145) * mm, "end": v(-462, 137) * mm});
            skLineSegment(sketch, "E164.3.0.53", {"start": v(-378, 337) * mm, "end": v(-378, 329) * mm});
            skLineSegment(sketch, "E164.3.0.54", {"start": v(-462, 295) * mm, "end": v(-454, 295) * mm});
            skLineSegment(sketch, "E164.3.0.55", {"start": v(-378, 179) * mm, "end": v(-378, 171) * mm});
            skLineSegment(sketch, "E164.3.0.56", {"start": v(-378, 58) * mm, "end": v(-386, 58) * mm});
            skLineSegment(sketch, "E164.3.0.57", {"start": v(-378, 66) * mm, "end": v(-378, 58) * mm});
            skLineSegment(sketch, "E164.3.0.58", {"start": v(-386, 179) * mm, "end": v(-386, 171) * mm});
            skLineSegment(sketch, "E164.3.0.59", {"start": v(-438, 379) * mm, "end": v(-430, 379) * mm});
            skLineSegment(sketch, "E164.3.0.60", {"start": v(-441, 64) * mm, "end": v(-441, 56) * mm});
            skLineSegment(sketch, "E164.3.0.61", {"start": v(-378, 66) * mm, "end": v(-386, 66) * mm});
            skLineSegment(sketch, "E164.3.0.62", {"start": v(-438, 221) * mm, "end": v(-438, 213) * mm});
            skLineSegment(sketch, "E164.3.0.63", {"start": v(-462, 179) * mm, "end": v(-462, 171) * mm});
            skLineSegment(sketch, "E164.3.0.64", {"start": v(-462, 66) * mm, "end": v(-454, 66) * mm});
            skLineSegment(sketch, "E164.3.0.65", {"start": v(-378, 171) * mm, "end": v(-386, 171) * mm});
            skLineSegment(sketch, "E164.3.0.66", {"start": v(-462, 171) * mm, "end": v(-454, 171) * mm});
            skLineSegment(sketch, "E164.3.0.67", {"start": v(-454, 66) * mm, "end": v(-454, 58) * mm});
            skLineSegment(sketch, "E164.3.0.68", {"start": v(-430, 221) * mm, "end": v(-430, 213) * mm});
            skLineSegment(sketch, "E164.3.0.69", {"start": v(-462, 145) * mm, "end": v(-454, 145) * mm});
            skLineSegment(sketch, "E164.3.0.70", {"start": v(-433, 64) * mm, "end": v(-433, 56) * mm});
            skLineSegment(sketch, "E164.3.0.71", {"start": v(-402, 379) * mm, "end": v(-410, 379) * mm});
            skLineSegment(sketch, "E164.3.0.72", {"start": v(-402, 253) * mm, "end": v(-410, 253) * mm});
            skLineSegment(sketch, "E164.3.0.73", {"start": v(-402, 359) * mm, "end": v(-410, 359) * mm});
            skLineSegment(sketch, "E164.3.0.74", {"start": v(-402, 201) * mm, "end": v(-402, 193) * mm});
            skLineSegment(sketch, "E164.3.0.75", {"start": v(-438, 201) * mm, "end": v(-438, 193) * mm});
            skLineSegment(sketch, "E164.3.0.76", {"start": v(-402, 221) * mm, "end": v(-402, 213) * mm});
            skLineSegment(sketch, "E164.3.0.77", {"start": v(-399, 173) * mm, "end": v(-407, 173) * mm});
            skLineSegment(sketch, "E164.3.0.78", {"start": v(-430, 201) * mm, "end": v(-430, 193) * mm});
            skLineSegment(sketch, "E164.3.0.79", {"start": v(-433, 301) * mm, "end": v(-433, 293) * mm});
            skLineSegment(sketch, "E164.3.0.80", {"start": v(-438, 253) * mm, "end": v(-430, 253) * mm});
            skLineSegment(sketch, "E164.3.0.81", {"start": v(-399, 56) * mm, "end": v(-407, 56) * mm});
            skLineSegment(sketch, "E164.3.0.82", {"start": v(-441, 143) * mm, "end": v(-433, 143) * mm});
            skLineSegment(sketch, "E164.3.0.83", {"start": v(-441, 173) * mm, "end": v(-433, 173) * mm});
            skLineSegment(sketch, "E164.3.0.84", {"start": v(-438, 36) * mm, "end": v(-430, 36) * mm});
            skLineSegment(sketch, "E164.3.0.85", {"start": v(-433, 181) * mm, "end": v(-433, 173) * mm});
            skLineSegment(sketch, "E164.3.0.86", {"start": v(-402, 24) * mm, "end": v(-410, 24) * mm});
            skLineSegment(sketch, "E164.3.0.87", {"start": v(-438, 123) * mm, "end": v(-430, 123) * mm});
            skLineSegment(sketch, "E164.3.0.88", {"start": v(-441, 181) * mm, "end": v(-433, 181) * mm});
            skLineSegment(sketch, "E164.3.0.89", {"start": v(-399, 181) * mm, "end": v(-399, 173) * mm});
            skLineSegment(sketch, "E164.3.0.90", {"start": v(-438, 193) * mm, "end": v(-430, 193) * mm});
            skLineSegment(sketch, "E164.3.0.91", {"start": v(-407, 181) * mm, "end": v(-407, 173) * mm});
            skLineSegment(sketch, "E164.3.0.92", {"start": v(-438, 123) * mm, "end": v(-438, 115) * mm});
            skLineSegment(sketch, "E164.3.0.93", {"start": v(-441, 143) * mm, "end": v(-441, 135) * mm});
            skLineSegment(sketch, "E164.3.0.94", {"start": v(-399, 64) * mm, "end": v(-399, 56) * mm});
            skLineSegment(sketch, "E164.3.0.95", {"start": v(-378, 337) * mm, "end": v(-386, 337) * mm});
            skLineSegment(sketch, "E164.3.0.96", {"start": v(-438, 44) * mm, "end": v(-430, 44) * mm});
            skLineSegment(sketch, "E164.3.0.97", {"start": v(-410, 379) * mm, "end": v(-410, 371) * mm});
            skLineSegment(sketch, "E164.3.0.98", {"start": v(-430, 24) * mm, "end": v(-430, 16) * mm});
            skLineSegment(sketch, "E164.3.0.99", {"start": v(-399, 181) * mm, "end": v(-407, 181) * mm});
            skLineSegment(sketch, "E164.3.0.100", {"start": v(-438, 359) * mm, "end": v(-430, 359) * mm});
            skLineSegment(sketch, "E164.3.0.101", {"start": v(-454, 179) * mm, "end": v(-454, 171) * mm});
            skLineSegment(sketch, "E164.3.0.102", {"start": v(-441, 64) * mm, "end": v(-433, 64) * mm});
            skLineSegment(sketch, "E164.3.0.103", {"start": v(-441, 181) * mm, "end": v(-441, 173) * mm});
            skLineSegment(sketch, "E164.3.0.104", {"start": v(-462, 179) * mm, "end": v(-454, 179) * mm});
            skLineSegment(sketch, "E164.3.0.105", {"start": v(-402, 201) * mm, "end": v(-410, 201) * mm});
            skLineSegment(sketch, "E164.3.0.106", {"start": v(-438, 24) * mm, "end": v(-438, 16) * mm});
            skLineSegment(sketch, "E164.3.0.107", {"start": v(-402, 24) * mm, "end": v(-402, 16) * mm});
            skLineSegment(sketch, "E164.3.0.108", {"start": v(-438, 213) * mm, "end": v(-430, 213) * mm});
            skLineSegment(sketch, "E164.3.0.109", {"start": v(-438, 24) * mm, "end": v(-430, 24) * mm});
            skLineSegment(sketch, "E164.3.0.110", {"start": v(-402, 103) * mm, "end": v(-402, 95) * mm});
            skLineSegment(sketch, "E164.3.0.111", {"start": v(-410, 44) * mm, "end": v(-410, 36) * mm});
            skLineSegment(sketch, "E164.3.0.112", {"start": v(-402, 261) * mm, "end": v(-402, 253) * mm});
            skLineSegment(sketch, "E164.3.0.113", {"start": v(-402, 379) * mm, "end": v(-402, 371) * mm});
            skLineSegment(sketch, "E164.3.0.114", {"start": v(-378, 179) * mm, "end": v(-386, 179) * mm});
            skLineSegment(sketch, "E164.3.0.115", {"start": v(-438, 44) * mm, "end": v(-438, 36) * mm});
            skLineSegment(sketch, "E164.3.0.116", {"start": v(-430, 44) * mm, "end": v(-430, 36) * mm});
            skLineSegment(sketch, "E164.3.0.117", {"start": v(-410, 261) * mm, "end": v(-410, 253) * mm});
            skLineSegment(sketch, "E164.3.0.118", {"start": v(-407, 64) * mm, "end": v(-407, 56) * mm});
            skLineSegment(sketch, "E164.3.0.119", {"start": v(-454, 303) * mm, "end": v(-454, 295) * mm});
            skLineSegment(sketch, "E164.3.0.120", {"start": v(-441, 135) * mm, "end": v(-433, 135) * mm});
            skLineSegment(sketch, "E164.3.0.121", {"start": v(-402, 193) * mm, "end": v(-410, 193) * mm});
            skLineSegment(sketch, "E164.3.0.122", {"start": v(-441, 301) * mm, "end": v(-441, 293) * mm});
            skLineSegment(sketch, "E164.3.0.123", {"start": v(-441, 56) * mm, "end": v(-433, 56) * mm});
            skLineSegment(sketch, "E164.3.0.124", {"start": v(-438, 371) * mm, "end": v(-430, 371) * mm});
            skLineSegment(sketch, "E164.3.0.125", {"start": v(-399, 64) * mm, "end": v(-407, 64) * mm});
            skLineSegment(sketch, "E164.3.0.126", {"start": v(-438, 379) * mm, "end": v(-438, 371) * mm});
            skLineSegment(sketch, "E164.3.0.127", {"start": v(-441, 301) * mm, "end": v(-433, 301) * mm});
            skLineSegment(sketch, "E164.3.0.128", {"start": v(-402, 44) * mm, "end": v(-402, 36) * mm});
            skLineSegment(sketch, "E164.3.0.129", {"start": v(-433, 143) * mm, "end": v(-433, 135) * mm});
            skLineSegment(sketch, "E164.3.0.130", {"start": v(-462, 137) * mm, "end": v(-454, 137) * mm});
            skLineSegment(sketch, "E164.3.0.131", {"start": v(-410, 103) * mm, "end": v(-410, 95) * mm});
            skLineSegment(sketch, "E164.3.0.132", {"start": v(-410, 24) * mm, "end": v(-410, 16) * mm});
            skLineSegment(sketch, "E164.3.0.133", {"start": v(-454, 145) * mm, "end": v(-454, 137) * mm});
            skLineSegment(sketch, "E164.3.0.134", {"start": v(-430, 379) * mm, "end": v(-430, 371) * mm});
            skLineSegment(sketch, "E164.3.0.135", {"start": v(-410, 221) * mm, "end": v(-410, 213) * mm});
            skLineSegment(sketch, "E164.3.0.136", {"start": v(-386, 66) * mm, "end": v(-386, 58) * mm});
            skLineSegment(sketch, "E164.3.0.137", {"start": v(-438, 351) * mm, "end": v(-430, 351) * mm});
            skLineSegment(sketch, "E164.3.0.138", {"start": v(-410, 359) * mm, "end": v(-410, 351) * mm});
            skLineSegment(sketch, "E164.3.0.139", {"start": v(-430, 103) * mm, "end": v(-430, 95) * mm});
            skLineSegment(sketch, "E164.3.0.140", {"start": v(-438, 115) * mm, "end": v(-430, 115) * mm});
            skLineSegment(sketch, "E164.3.0.141", {"start": v(-402, 371) * mm, "end": v(-410, 371) * mm});
            skLineSegment(sketch, "E164.3.0.142", {"start": v(-402, 36) * mm, "end": v(-410, 36) * mm});
            skLineSegment(sketch, "E164.3.0.143", {"start": v(-441, 331) * mm, "end": v(-433, 331) * mm});
            skLineSegment(sketch, "E164.3.0.144", {"start": v(-399, 143) * mm, "end": v(-399, 135) * mm});
            skLineSegment(sketch, "E164.3.0.145", {"start": v(-399, 331) * mm, "end": v(-407, 331) * mm});
            skLineSegment(sketch, "E164.3.0.146", {"start": v(-378, 145) * mm, "end": v(-378, 137) * mm});
            skLineSegment(sketch, "E164.3.0.147", {"start": v(-430, 261) * mm, "end": v(-430, 253) * mm});
            skLineSegment(sketch, "E164.3.0.148", {"start": v(-407, 339) * mm, "end": v(-407, 331) * mm});
            skLineSegment(sketch, "E164.3.0.149", {"start": v(-438, 261) * mm, "end": v(-438, 253) * mm});
            skLineSegment(sketch, "E164.3.0.150", {"start": v(-438, 359) * mm, "end": v(-438, 351) * mm});
            skLineSegment(sketch, "E164.3.0.151", {"start": v(-399, 135) * mm, "end": v(-407, 135) * mm});
            skLineSegment(sketch, "E164.3.0.152", {"start": v(-407, 301) * mm, "end": v(-407, 293) * mm});
            skLineSegment(sketch, "E164.3.0.153", {"start": v(-386, 337) * mm, "end": v(-386, 329) * mm});
            skLineSegment(sketch, "E164.3.0.154", {"start": v(-441, 293) * mm, "end": v(-433, 293) * mm});
            skLineSegment(sketch, "E164.3.0.155", {"start": v(-454, 337) * mm, "end": v(-454, 329) * mm});
            skLineSegment(sketch, "E164.3.0.156", {"start": v(-438, 103) * mm, "end": v(-438, 95) * mm});
            skLineSegment(sketch, "E164.3.0.157", {"start": v(-433, 339) * mm, "end": v(-433, 331) * mm});
            skLineSegment(sketch, "E164.3.0.158", {"start": v(-399, 293) * mm, "end": v(-407, 293) * mm});
            skLineSegment(sketch, "E164.3.0.159", {"start": v(-402, 103) * mm, "end": v(-410, 103) * mm});
            skLineSegment(sketch, "E164.3.0.160", {"start": v(-402, 16) * mm, "end": v(-410, 16) * mm});
            skLineSegment(sketch, "E164.3.0.161", {"start": v(-402, 359) * mm, "end": v(-402, 351) * mm});
            skLineSegment(sketch, "E164.3.0.162", {"start": v(-438, 95) * mm, "end": v(-430, 95) * mm});
            skLineSegment(sketch, "E164.3.0.163", {"start": v(-386, 303) * mm, "end": v(-386, 295) * mm});
            skLineSegment(sketch, "E164.3.0.164", {"start": v(-402, 123) * mm, "end": v(-402, 115) * mm});
            skLineSegment(sketch, "E164.3.0.165", {"start": v(-386, 145) * mm, "end": v(-386, 137) * mm});
            skLineSegment(sketch, "E164.3.0.166", {"start": v(-402, 115) * mm, "end": v(-410, 115) * mm});
            skLineSegment(sketch, "E164.3.0.167", {"start": v(-438, 16) * mm, "end": v(-430, 16) * mm});
            skLineSegment(sketch, "E164.3.0.168", {"start": v(-402, 281) * mm, "end": v(-402, 273) * mm});
            skLineSegment(sketch, "E164.3.0.169", {"start": v(-378, 303) * mm, "end": v(-378, 295) * mm});
            skLineSegment(sketch, "E164.3.0.170", {"start": v(-430, 123) * mm, "end": v(-430, 115) * mm});
            skLineSegment(sketch, "E164.3.0.171", {"start": v(-399, 339) * mm, "end": v(-407, 339) * mm});
            skLineSegment(sketch, "E164.3.0.172", {"start": v(-402, 123) * mm, "end": v(-410, 123) * mm});
            skLineSegment(sketch, "E164.3.0.173", {"start": v(-402, 273) * mm, "end": v(-410, 273) * mm});
            skLineSegment(sketch, "E164.3.0.174", {"start": v(-438, 281) * mm, "end": v(-438, 273) * mm});
            skLineSegment(sketch, "E164.3.0.175", {"start": v(-402, 261) * mm, "end": v(-410, 261) * mm});
            skLineSegment(sketch, "E164.3.0.176", {"start": v(-430, 359) * mm, "end": v(-430, 351) * mm});
            skLineSegment(sketch, "E164.3.0.177", {"start": v(-399, 143) * mm, "end": v(-407, 143) * mm});
            skLineSegment(sketch, "E164.3.0.178", {"start": v(-410, 201) * mm, "end": v(-410, 193) * mm});
            skLineSegment(sketch, "E164.3.0.179", {"start": v(-407, 143) * mm, "end": v(-407, 135) * mm});
            skLineSegment(sketch, "E164.3.0.180", {"start": v(-399, 301) * mm, "end": v(-399, 293) * mm});
            skLineSegment(sketch, "E164.3.0.181", {"start": v(-378, 145) * mm, "end": v(-386, 145) * mm});
            skLineSegment(sketch, "E164.3.0.182", {"start": v(-399, 301) * mm, "end": v(-407, 301) * mm});
            skLineSegment(sketch, "E164.3.0.183", {"start": v(-438, 273) * mm, "end": v(-430, 273) * mm});
            skLineSegment(sketch, "E164.3.0.184", {"start": v(-438, 261) * mm, "end": v(-430, 261) * mm});
            skLineSegment(sketch, "E164.3.0.185", {"start": v(-438, 281) * mm, "end": v(-430, 281) * mm});
            skLineSegment(sketch, "E164.3.0.186", {"start": v(-378, 303) * mm, "end": v(-386, 303) * mm});
            skLineSegment(sketch, "E164.3.0.187", {"start": v(-402, 281) * mm, "end": v(-410, 281) * mm});
            skLineSegment(sketch, "E164.3.0.188", {"start": v(-441, 339) * mm, "end": v(-441, 331) * mm});
            skLineSegment(sketch, "E164.3.0.189", {"start": v(-402, 351) * mm, "end": v(-410, 351) * mm});
            skLineSegment(sketch, "E164.3.0.190", {"start": v(-402, 213) * mm, "end": v(-410, 213) * mm});
            skLineSegment(sketch, "E164.3.0.191", {"start": v(-402, 44) * mm, "end": v(-410, 44) * mm});
            skLineSegment(sketch, "E164.3.0.192", {"start": v(-410, 281) * mm, "end": v(-410, 273) * mm});
            skLineSegment(sketch, "E164.3.0.193", {"start": v(-410, 123) * mm, "end": v(-410, 115) * mm});
            skLineSegment(sketch, "E164.3.0.194", {"start": v(-441, 339) * mm, "end": v(-433, 339) * mm});
            skLineSegment(sketch, "E164.3.0.195", {"start": v(-378, 137) * mm, "end": v(-386, 137) * mm});
            skLineSegment(sketch, "E164.3.0.196", {"start": v(-378, 295) * mm, "end": v(-386, 295) * mm});
            skLineSegment(sketch, "E164.3.0.197", {"start": v(-399, 339) * mm, "end": v(-399, 331) * mm});
            skLineSegment(sketch, "E164.3.0.198", {"start": v(-438, 103) * mm, "end": v(-430, 103) * mm});
            skLineSegment(sketch, "E164.3.0.199", {"start": v(-430, 281) * mm, "end": v(-430, 273) * mm});
            skPoint(sketch, "E164.4.0.0", {"position": v(-526, 197) * mm});
            skPoint(sketch, "E164.4.0.1", {"position": v(-554, 119) * mm});
            skPoint(sketch, "E164.4.0.2", {"position": v(-526, 119) * mm});
            skPoint(sketch, "E164.4.0.3", {"position": v(-502, 175) * mm});
            skPoint(sketch, "E164.4.0.4", {"position": v(-578, 299) * mm});
            skPoint(sketch, "E164.4.0.5", {"position": v(-578, 141) * mm});
            skPoint(sketch, "E164.4.0.6", {"position": v(-554, 217) * mm});
            skPoint(sketch, "E164.4.0.7", {"position": v(-554, 375) * mm});
            skPoint(sketch, "E164.4.0.8", {"position": v(-557, 60) * mm});
            skPoint(sketch, "E164.4.0.9", {"position": v(-578, 333) * mm});
            skPoint(sketch, "E164.4.0.10", {"position": v(-523, 335) * mm});
            skPoint(sketch, "E164.4.0.11", {"position": v(-554, 99) * mm});
            skPoint(sketch, "E164.4.0.12", {"position": v(-502, 333) * mm});
            skPoint(sketch, "E164.4.0.13", {"position": v(-554, 277) * mm});
            skPoint(sketch, "E164.4.0.14", {"position": v(-526, 217) * mm});
            skPoint(sketch, "E164.4.0.15", {"position": v(-554, 257) * mm});
            skPoint(sketch, "E164.4.0.16", {"position": v(-578, 175) * mm});
            skPoint(sketch, "E164.4.0.17", {"position": v(-526, 40) * mm});
            skPoint(sketch, "E164.4.0.18", {"position": v(-523, 60) * mm});
            skPoint(sketch, "E164.4.0.19", {"position": v(-578, 62) * mm});
            skPoint(sketch, "E164.4.0.20", {"position": v(-523, 177) * mm});
            skPoint(sketch, "E164.4.0.21", {"position": v(-526, 99) * mm});
            skPoint(sketch, "E164.4.0.22", {"position": v(-557, 177) * mm});
            skPoint(sketch, "E164.4.0.23", {"position": v(-554, 355) * mm});
            skPoint(sketch, "E164.4.0.24", {"position": v(-554, 197) * mm});
            skPoint(sketch, "E164.4.0.25", {"position": v(-526, 257) * mm});
            skPoint(sketch, "E164.4.0.26", {"position": v(-554, 20) * mm});
            skPoint(sketch, "E164.4.0.27", {"position": v(-502, 62) * mm});
            skPoint(sketch, "E164.4.0.28", {"position": v(-526, 375) * mm});
            skPoint(sketch, "E164.4.0.29", {"position": v(-557, 297) * mm});
            skPoint(sketch, "E164.4.0.30", {"position": v(-523, 297) * mm});
            skPoint(sketch, "E164.4.0.31", {"position": v(-554, 40) * mm});
            skPoint(sketch, "E164.4.0.32", {"position": v(-502, 141) * mm});
            skPoint(sketch, "E164.4.0.33", {"position": v(-557, 335) * mm});
            skPoint(sketch, "E164.4.0.34", {"position": v(-526, 20) * mm});
            skPoint(sketch, "E164.4.0.35", {"position": v(-526, 277) * mm});
            skPoint(sketch, "E164.4.0.36", {"position": v(-502, 299) * mm});
            skPoint(sketch, "E164.4.0.37", {"position": v(-557, 139) * mm});
            skPoint(sketch, "E164.4.0.38", {"position": v(-526, 355) * mm});
            skPoint(sketch, "E164.4.0.39", {"position": v(-523, 139) * mm});
            skLineSegment(sketch, "E164.4.0.40", {"start": v(-582, 337) * mm, "end": v(-574, 337) * mm});
            skLineSegment(sketch, "E164.4.0.41", {"start": v(-582, 337) * mm, "end": v(-582, 329) * mm});
            skLineSegment(sketch, "E164.4.0.42", {"start": v(-582, 329) * mm, "end": v(-574, 329) * mm});
            skLineSegment(sketch, "E164.4.0.43", {"start": v(-498, 329) * mm, "end": v(-506, 329) * mm});
            skLineSegment(sketch, "E164.4.0.44", {"start": v(-522, 95) * mm, "end": v(-530, 95) * mm});
            skLineSegment(sketch, "E164.4.0.45", {"start": v(-558, 221) * mm, "end": v(-550, 221) * mm});
            skLineSegment(sketch, "E164.4.0.46", {"start": v(-582, 66) * mm, "end": v(-582, 58) * mm});
            skLineSegment(sketch, "E164.4.0.47", {"start": v(-522, 221) * mm, "end": v(-530, 221) * mm});
            skLineSegment(sketch, "E164.4.0.48", {"start": v(-582, 58) * mm, "end": v(-574, 58) * mm});
            skLineSegment(sketch, "E164.4.0.49", {"start": v(-558, 201) * mm, "end": v(-550, 201) * mm});
            skLineSegment(sketch, "E164.4.0.50", {"start": v(-582, 303) * mm, "end": v(-574, 303) * mm});
            skLineSegment(sketch, "E164.4.0.51", {"start": v(-582, 303) * mm, "end": v(-582, 295) * mm});
            skLineSegment(sketch, "E164.4.0.52", {"start": v(-582, 145) * mm, "end": v(-582, 137) * mm});
            skLineSegment(sketch, "E164.4.0.53", {"start": v(-498, 337) * mm, "end": v(-498, 329) * mm});
            skLineSegment(sketch, "E164.4.0.54", {"start": v(-582, 295) * mm, "end": v(-574, 295) * mm});
            skLineSegment(sketch, "E164.4.0.55", {"start": v(-498, 179) * mm, "end": v(-498, 171) * mm});
            skLineSegment(sketch, "E164.4.0.56", {"start": v(-498, 58) * mm, "end": v(-506, 58) * mm});
            skLineSegment(sketch, "E164.4.0.57", {"start": v(-498, 66) * mm, "end": v(-498, 58) * mm});
            skLineSegment(sketch, "E164.4.0.58", {"start": v(-506, 179) * mm, "end": v(-506, 171) * mm});
            skLineSegment(sketch, "E164.4.0.59", {"start": v(-558, 379) * mm, "end": v(-550, 379) * mm});
            skLineSegment(sketch, "E164.4.0.60", {"start": v(-561, 64) * mm, "end": v(-561, 56) * mm});
            skLineSegment(sketch, "E164.4.0.61", {"start": v(-498, 66) * mm, "end": v(-506, 66) * mm});
            skLineSegment(sketch, "E164.4.0.62", {"start": v(-558, 221) * mm, "end": v(-558, 213) * mm});
            skLineSegment(sketch, "E164.4.0.63", {"start": v(-582, 179) * mm, "end": v(-582, 171) * mm});
            skLineSegment(sketch, "E164.4.0.64", {"start": v(-582, 66) * mm, "end": v(-574, 66) * mm});
            skLineSegment(sketch, "E164.4.0.65", {"start": v(-498, 171) * mm, "end": v(-506, 171) * mm});
            skLineSegment(sketch, "E164.4.0.66", {"start": v(-582, 171) * mm, "end": v(-574, 171) * mm});
            skLineSegment(sketch, "E164.4.0.67", {"start": v(-574, 66) * mm, "end": v(-574, 58) * mm});
            skLineSegment(sketch, "E164.4.0.68", {"start": v(-550, 221) * mm, "end": v(-550, 213) * mm});
            skLineSegment(sketch, "E164.4.0.69", {"start": v(-582, 145) * mm, "end": v(-574, 145) * mm});
            skLineSegment(sketch, "E164.4.0.70", {"start": v(-553, 64) * mm, "end": v(-553, 56) * mm});
            skLineSegment(sketch, "E164.4.0.71", {"start": v(-522, 379) * mm, "end": v(-530, 379) * mm});
            skLineSegment(sketch, "E164.4.0.72", {"start": v(-522, 253) * mm, "end": v(-530, 253) * mm});
            skLineSegment(sketch, "E164.4.0.73", {"start": v(-522, 359) * mm, "end": v(-530, 359) * mm});
            skLineSegment(sketch, "E164.4.0.74", {"start": v(-522, 201) * mm, "end": v(-522, 193) * mm});
            skLineSegment(sketch, "E164.4.0.75", {"start": v(-558, 201) * mm, "end": v(-558, 193) * mm});
            skLineSegment(sketch, "E164.4.0.76", {"start": v(-522, 221) * mm, "end": v(-522, 213) * mm});
            skLineSegment(sketch, "E164.4.0.77", {"start": v(-519, 173) * mm, "end": v(-527, 173) * mm});
            skLineSegment(sketch, "E164.4.0.78", {"start": v(-550, 201) * mm, "end": v(-550, 193) * mm});
            skLineSegment(sketch, "E164.4.0.79", {"start": v(-553, 301) * mm, "end": v(-553, 293) * mm});
            skLineSegment(sketch, "E164.4.0.80", {"start": v(-558, 253) * mm, "end": v(-550, 253) * mm});
            skLineSegment(sketch, "E164.4.0.81", {"start": v(-519, 56) * mm, "end": v(-527, 56) * mm});
            skLineSegment(sketch, "E164.4.0.82", {"start": v(-561, 143) * mm, "end": v(-553, 143) * mm});
            skLineSegment(sketch, "E164.4.0.83", {"start": v(-561, 173) * mm, "end": v(-553, 173) * mm});
            skLineSegment(sketch, "E164.4.0.84", {"start": v(-558, 36) * mm, "end": v(-550, 36) * mm});
            skLineSegment(sketch, "E164.4.0.85", {"start": v(-553, 181) * mm, "end": v(-553, 173) * mm});
            skLineSegment(sketch, "E164.4.0.86", {"start": v(-522, 24) * mm, "end": v(-530, 24) * mm});
            skLineSegment(sketch, "E164.4.0.87", {"start": v(-558, 123) * mm, "end": v(-550, 123) * mm});
            skLineSegment(sketch, "E164.4.0.88", {"start": v(-561, 181) * mm, "end": v(-553, 181) * mm});
            skLineSegment(sketch, "E164.4.0.89", {"start": v(-519, 181) * mm, "end": v(-519, 173) * mm});
            skLineSegment(sketch, "E164.4.0.90", {"start": v(-558, 193) * mm, "end": v(-550, 193) * mm});
            skLineSegment(sketch, "E164.4.0.91", {"start": v(-527, 181) * mm, "end": v(-527, 173) * mm});
            skLineSegment(sketch, "E164.4.0.92", {"start": v(-558, 123) * mm, "end": v(-558, 115) * mm});
            skLineSegment(sketch, "E164.4.0.93", {"start": v(-561, 143) * mm, "end": v(-561, 135) * mm});
            skLineSegment(sketch, "E164.4.0.94", {"start": v(-519, 64) * mm, "end": v(-519, 56) * mm});
            skLineSegment(sketch, "E164.4.0.95", {"start": v(-498, 337) * mm, "end": v(-506, 337) * mm});
            skLineSegment(sketch, "E164.4.0.96", {"start": v(-558, 44) * mm, "end": v(-550, 44) * mm});
            skLineSegment(sketch, "E164.4.0.97", {"start": v(-530, 379) * mm, "end": v(-530, 371) * mm});
            skLineSegment(sketch, "E164.4.0.98", {"start": v(-550, 24) * mm, "end": v(-550, 16) * mm});
            skLineSegment(sketch, "E164.4.0.99", {"start": v(-519, 181) * mm, "end": v(-527, 181) * mm});
            skLineSegment(sketch, "E164.4.0.100", {"start": v(-558, 359) * mm, "end": v(-550, 359) * mm});
            skLineSegment(sketch, "E164.4.0.101", {"start": v(-574, 179) * mm, "end": v(-574, 171) * mm});
            skLineSegment(sketch, "E164.4.0.102", {"start": v(-561, 64) * mm, "end": v(-553, 64) * mm});
            skLineSegment(sketch, "E164.4.0.103", {"start": v(-561, 181) * mm, "end": v(-561, 173) * mm});
            skLineSegment(sketch, "E164.4.0.104", {"start": v(-582, 179) * mm, "end": v(-574, 179) * mm});
            skLineSegment(sketch, "E164.4.0.105", {"start": v(-522, 201) * mm, "end": v(-530, 201) * mm});
            skLineSegment(sketch, "E164.4.0.106", {"start": v(-558, 24) * mm, "end": v(-558, 16) * mm});
            skLineSegment(sketch, "E164.4.0.107", {"start": v(-522, 24) * mm, "end": v(-522, 16) * mm});
            skLineSegment(sketch, "E164.4.0.108", {"start": v(-558, 213) * mm, "end": v(-550, 213) * mm});
            skLineSegment(sketch, "E164.4.0.109", {"start": v(-558, 24) * mm, "end": v(-550, 24) * mm});
            skLineSegment(sketch, "E164.4.0.110", {"start": v(-522, 103) * mm, "end": v(-522, 95) * mm});
            skLineSegment(sketch, "E164.4.0.111", {"start": v(-530, 44) * mm, "end": v(-530, 36) * mm});
            skLineSegment(sketch, "E164.4.0.112", {"start": v(-522, 261) * mm, "end": v(-522, 253) * mm});
            skLineSegment(sketch, "E164.4.0.113", {"start": v(-522, 379) * mm, "end": v(-522, 371) * mm});
            skLineSegment(sketch, "E164.4.0.114", {"start": v(-498, 179) * mm, "end": v(-506, 179) * mm});
            skLineSegment(sketch, "E164.4.0.115", {"start": v(-558, 44) * mm, "end": v(-558, 36) * mm});
            skLineSegment(sketch, "E164.4.0.116", {"start": v(-550, 44) * mm, "end": v(-550, 36) * mm});
            skLineSegment(sketch, "E164.4.0.117", {"start": v(-530, 261) * mm, "end": v(-530, 253) * mm});
            skLineSegment(sketch, "E164.4.0.118", {"start": v(-527, 64) * mm, "end": v(-527, 56) * mm});
            skLineSegment(sketch, "E164.4.0.119", {"start": v(-574, 303) * mm, "end": v(-574, 295) * mm});
            skLineSegment(sketch, "E164.4.0.120", {"start": v(-561, 135) * mm, "end": v(-553, 135) * mm});
            skLineSegment(sketch, "E164.4.0.121", {"start": v(-522, 193) * mm, "end": v(-530, 193) * mm});
            skLineSegment(sketch, "E164.4.0.122", {"start": v(-561, 301) * mm, "end": v(-561, 293) * mm});
            skLineSegment(sketch, "E164.4.0.123", {"start": v(-561, 56) * mm, "end": v(-553, 56) * mm});
            skLineSegment(sketch, "E164.4.0.124", {"start": v(-558, 371) * mm, "end": v(-550, 371) * mm});
            skLineSegment(sketch, "E164.4.0.125", {"start": v(-519, 64) * mm, "end": v(-527, 64) * mm});
            skLineSegment(sketch, "E164.4.0.126", {"start": v(-558, 379) * mm, "end": v(-558, 371) * mm});
            skLineSegment(sketch, "E164.4.0.127", {"start": v(-561, 301) * mm, "end": v(-553, 301) * mm});
            skLineSegment(sketch, "E164.4.0.128", {"start": v(-522, 44) * mm, "end": v(-522, 36) * mm});
            skLineSegment(sketch, "E164.4.0.129", {"start": v(-553, 143) * mm, "end": v(-553, 135) * mm});
            skLineSegment(sketch, "E164.4.0.130", {"start": v(-582, 137) * mm, "end": v(-574, 137) * mm});
            skLineSegment(sketch, "E164.4.0.131", {"start": v(-530, 103) * mm, "end": v(-530, 95) * mm});
            skLineSegment(sketch, "E164.4.0.132", {"start": v(-530, 24) * mm, "end": v(-530, 16) * mm});
            skLineSegment(sketch, "E164.4.0.133", {"start": v(-574, 145) * mm, "end": v(-574, 137) * mm});
            skLineSegment(sketch, "E164.4.0.134", {"start": v(-550, 379) * mm, "end": v(-550, 371) * mm});
            skLineSegment(sketch, "E164.4.0.135", {"start": v(-530, 221) * mm, "end": v(-530, 213) * mm});
            skLineSegment(sketch, "E164.4.0.136", {"start": v(-506, 66) * mm, "end": v(-506, 58) * mm});
            skLineSegment(sketch, "E164.4.0.137", {"start": v(-558, 351) * mm, "end": v(-550, 351) * mm});
            skLineSegment(sketch, "E164.4.0.138", {"start": v(-530, 359) * mm, "end": v(-530, 351) * mm});
            skLineSegment(sketch, "E164.4.0.139", {"start": v(-550, 103) * mm, "end": v(-550, 95) * mm});
            skLineSegment(sketch, "E164.4.0.140", {"start": v(-558, 115) * mm, "end": v(-550, 115) * mm});
            skLineSegment(sketch, "E164.4.0.141", {"start": v(-522, 371) * mm, "end": v(-530, 371) * mm});
            skLineSegment(sketch, "E164.4.0.142", {"start": v(-522, 36) * mm, "end": v(-530, 36) * mm});
            skLineSegment(sketch, "E164.4.0.143", {"start": v(-561, 331) * mm, "end": v(-553, 331) * mm});
            skLineSegment(sketch, "E164.4.0.144", {"start": v(-519, 143) * mm, "end": v(-519, 135) * mm});
            skLineSegment(sketch, "E164.4.0.145", {"start": v(-519, 331) * mm, "end": v(-527, 331) * mm});
            skLineSegment(sketch, "E164.4.0.146", {"start": v(-498, 145) * mm, "end": v(-498, 137) * mm});
            skLineSegment(sketch, "E164.4.0.147", {"start": v(-550, 261) * mm, "end": v(-550, 253) * mm});
            skLineSegment(sketch, "E164.4.0.148", {"start": v(-527, 339) * mm, "end": v(-527, 331) * mm});
            skLineSegment(sketch, "E164.4.0.149", {"start": v(-558, 261) * mm, "end": v(-558, 253) * mm});
            skLineSegment(sketch, "E164.4.0.150", {"start": v(-558, 359) * mm, "end": v(-558, 351) * mm});
            skLineSegment(sketch, "E164.4.0.151", {"start": v(-519, 135) * mm, "end": v(-527, 135) * mm});
            skLineSegment(sketch, "E164.4.0.152", {"start": v(-527, 301) * mm, "end": v(-527, 293) * mm});
            skLineSegment(sketch, "E164.4.0.153", {"start": v(-506, 337) * mm, "end": v(-506, 329) * mm});
            skLineSegment(sketch, "E164.4.0.154", {"start": v(-561, 293) * mm, "end": v(-553, 293) * mm});
            skLineSegment(sketch, "E164.4.0.155", {"start": v(-574, 337) * mm, "end": v(-574, 329) * mm});
            skLineSegment(sketch, "E164.4.0.156", {"start": v(-558, 103) * mm, "end": v(-558, 95) * mm});
            skLineSegment(sketch, "E164.4.0.157", {"start": v(-553, 339) * mm, "end": v(-553, 331) * mm});
            skLineSegment(sketch, "E164.4.0.158", {"start": v(-519, 293) * mm, "end": v(-527, 293) * mm});
            skLineSegment(sketch, "E164.4.0.159", {"start": v(-522, 103) * mm, "end": v(-530, 103) * mm});
            skLineSegment(sketch, "E164.4.0.160", {"start": v(-522, 16) * mm, "end": v(-530, 16) * mm});
            skLineSegment(sketch, "E164.4.0.161", {"start": v(-522, 359) * mm, "end": v(-522, 351) * mm});
            skLineSegment(sketch, "E164.4.0.162", {"start": v(-558, 95) * mm, "end": v(-550, 95) * mm});
            skLineSegment(sketch, "E164.4.0.163", {"start": v(-506, 303) * mm, "end": v(-506, 295) * mm});
            skLineSegment(sketch, "E164.4.0.164", {"start": v(-522, 123) * mm, "end": v(-522, 115) * mm});
            skLineSegment(sketch, "E164.4.0.165", {"start": v(-506, 145) * mm, "end": v(-506, 137) * mm});
            skLineSegment(sketch, "E164.4.0.166", {"start": v(-522, 115) * mm, "end": v(-530, 115) * mm});
            skLineSegment(sketch, "E164.4.0.167", {"start": v(-558, 16) * mm, "end": v(-550, 16) * mm});
            skLineSegment(sketch, "E164.4.0.168", {"start": v(-522, 281) * mm, "end": v(-522, 273) * mm});
            skLineSegment(sketch, "E164.4.0.169", {"start": v(-498, 303) * mm, "end": v(-498, 295) * mm});
            skLineSegment(sketch, "E164.4.0.170", {"start": v(-550, 123) * mm, "end": v(-550, 115) * mm});
            skLineSegment(sketch, "E164.4.0.171", {"start": v(-519, 339) * mm, "end": v(-527, 339) * mm});
            skLineSegment(sketch, "E164.4.0.172", {"start": v(-522, 123) * mm, "end": v(-530, 123) * mm});
            skLineSegment(sketch, "E164.4.0.173", {"start": v(-522, 273) * mm, "end": v(-530, 273) * mm});
            skLineSegment(sketch, "E164.4.0.174", {"start": v(-558, 281) * mm, "end": v(-558, 273) * mm});
            skLineSegment(sketch, "E164.4.0.175", {"start": v(-522, 261) * mm, "end": v(-530, 261) * mm});
            skLineSegment(sketch, "E164.4.0.176", {"start": v(-550, 359) * mm, "end": v(-550, 351) * mm});
            skLineSegment(sketch, "E164.4.0.177", {"start": v(-519, 143) * mm, "end": v(-527, 143) * mm});
            skLineSegment(sketch, "E164.4.0.178", {"start": v(-530, 201) * mm, "end": v(-530, 193) * mm});
            skLineSegment(sketch, "E164.4.0.179", {"start": v(-527, 143) * mm, "end": v(-527, 135) * mm});
            skLineSegment(sketch, "E164.4.0.180", {"start": v(-519, 301) * mm, "end": v(-519, 293) * mm});
            skLineSegment(sketch, "E164.4.0.181", {"start": v(-498, 145) * mm, "end": v(-506, 145) * mm});
            skLineSegment(sketch, "E164.4.0.182", {"start": v(-519, 301) * mm, "end": v(-527, 301) * mm});
            skLineSegment(sketch, "E164.4.0.183", {"start": v(-558, 273) * mm, "end": v(-550, 273) * mm});
            skLineSegment(sketch, "E164.4.0.184", {"start": v(-558, 261) * mm, "end": v(-550, 261) * mm});
            skLineSegment(sketch, "E164.4.0.185", {"start": v(-558, 281) * mm, "end": v(-550, 281) * mm});
            skLineSegment(sketch, "E164.4.0.186", {"start": v(-498, 303) * mm, "end": v(-506, 303) * mm});
            skLineSegment(sketch, "E164.4.0.187", {"start": v(-522, 281) * mm, "end": v(-530, 281) * mm});
            skLineSegment(sketch, "E164.4.0.188", {"start": v(-561, 339) * mm, "end": v(-561, 331) * mm});
            skLineSegment(sketch, "E164.4.0.189", {"start": v(-522, 351) * mm, "end": v(-530, 351) * mm});
            skLineSegment(sketch, "E164.4.0.190", {"start": v(-522, 213) * mm, "end": v(-530, 213) * mm});
            skLineSegment(sketch, "E164.4.0.191", {"start": v(-522, 44) * mm, "end": v(-530, 44) * mm});
            skLineSegment(sketch, "E164.4.0.192", {"start": v(-530, 281) * mm, "end": v(-530, 273) * mm});
            skLineSegment(sketch, "E164.4.0.193", {"start": v(-530, 123) * mm, "end": v(-530, 115) * mm});
            skLineSegment(sketch, "E164.4.0.194", {"start": v(-561, 339) * mm, "end": v(-553, 339) * mm});
            skLineSegment(sketch, "E164.4.0.195", {"start": v(-498, 137) * mm, "end": v(-506, 137) * mm});
            skLineSegment(sketch, "E164.4.0.196", {"start": v(-498, 295) * mm, "end": v(-506, 295) * mm});
            skLineSegment(sketch, "E164.4.0.197", {"start": v(-519, 339) * mm, "end": v(-519, 331) * mm});
            skLineSegment(sketch, "E164.4.0.198", {"start": v(-558, 103) * mm, "end": v(-550, 103) * mm});
            skLineSegment(sketch, "E164.4.0.199", {"start": v(-550, 281) * mm, "end": v(-550, 273) * mm});
            skLineSegment(sketch, "E164.direction1", {"start": v(-78, 16) * mm, "end": v(-198, 16) * mm, "construction": true});
            skSolve(sketch);
        }
        {
            var Q0;
            Q0 = qSketchRegion(id + "F2", true);
            extrude(context, id + "F3", {"entities" : qUnion([Q0]), "operationType" : NewBodyOperationType.ADD, "depth" : 15 * mm, "offsetDistance" : 25 * mm});
        }
        {
            var Q0;
            Q0=sQuery(id+"F0.wireOp",VERTEX,"E43.3.0.28");
            var Q1;
            Q1=sQuery(id+"F0.wireOp",VERTEX,"E43.2.0.31");
            var Q2;
            Q2=sQuery(id+"F0.wireOp",VERTEX,"E43.2.0.8");
            var Q3;
            Q3=sQuery(id+"F0.wireOp",VERTEX,"E12.MirrorP");
            var Q4;
            Q4=sQuery(id+"F0.wireOp",VERTEX,"E43.3.0.6");
            var Q5;
            Q5=sQuery(id+"F0.wireOp",VERTEX,"E43.2.0.38");
            var Q6;
            Q6=sQuery(id+"F0.wireOp",VERTEX,"E43.3.0.17");
            var Q7;
            Q7=sQuery(id+"F0.wireOp",VERTEX,"E43.4.0.4");
            var Q8;
            Q8=sQuery(id+"F0.wireOp",VERTEX,"E43.1.0.13");
            var Q9;
            Q9=sQuery(id+"F0.wireOp",VERTEX,"E43.2.0.4");
            var Q10;
            Q10=sQuery(id+"F0.wireOp",VERTEX,"E43.4.0.38");
            var Q11;
            Q11=sQuery(id+"F0.wireOp",VERTEX,"E36.MirrorP");
            var Q12;
            Q12=sQuery(id+"F0.wireOp",VERTEX,"E43.1.0.5");
            var Q13;
            Q13=sQuery(id+"F0.wireOp",VERTEX,"E43.3.0.9");
            var Q14;
            Q14=sQuery(id+"F0.wireOp",VERTEX,"E43.4.0.0");
            var Q15;
            Q15=sQuery(id+"F0.wireOp",VERTEX,"E43.3.0.5");
            var Q16;
            Q16=sQuery(id+"F0.wireOp",VERTEX,"E43.4.0.28");
            var Q17;
            Q17=sQuery(id+"F0.wireOp",VERTEX,"E43.4.0.17");
            var Q18;
            Q18=sQuery(id+"F0.wireOp",VERTEX,"E38.MirrorP");
            var Q19;
            Q19=sQuery(id+"F0.wireOp",VERTEX,"E33.MirrorP");
            var Q20;
            Q20=sQuery(id+"F0.wireOp",VERTEX,"E43.2.0.21");
            var Q21;
            Q21=sQuery(id+"F0.wireOp",VERTEX,"E42.MirrorP");
            var Q22;
            Q22=sQuery(id+"F0.wireOp",VERTEX,"E43.3.0.39");
            var Q23;
            Q23=sQuery(id+"F0.wireOp",VERTEX,"E43.1.0.39");
            var Q24;
            Q24=sQuery(id+"F0.wireOp",VERTEX,"E43.3.0.8");
            var Q25;
            Q25=sQuery(id+"F0.wireOp",VERTEX,"E43.2.0.39");
            var Q26;
            Q26=sQuery(id+"F0.wireOp",VERTEX,"E35.MirrorP");
            var Q27;
            Q27=sQuery(id+"F0.wireOp",VERTEX,"E43.1.0.9");
            var Q28;
            Q28=sQuery(id+"F0.wireOp",VERTEX,"E43.2.0.1");
            var Q29;
            Q29=sQuery(id+"F0.wireOp",VERTEX,"E43.3.0.7");
            var Q30;
            Q30=sQuery(id+"F0.wireOp",VERTEX,"E43.3.0.38");
            var Q31;
            Q31=sQuery(id+"F0.wireOp",VERTEX,"E13.MirrorP");
            var Q32;
            Q32=sQuery(id+"F0.wireOp",VERTEX,"E19.MirrorP");
            var Q33;
            Q33=sQuery(id+"F0.wireOp",VERTEX,"E15.MirrorP");
            var Q34;
            Q34=sQuery(id+"F0.wireOp",VERTEX,"E43.1.0.6");
            var Q35;
            Q35=sQuery(id+"F0.wireOp",VERTEX,"E43.1.0.30");
            var Q36;
            Q36=sQuery(id+"F0.wireOp",VERTEX,"E16.MirrorP");
            var Q37;
            Q37=sQuery(id+"F0.wireOp",VERTEX,"E43.1.0.21");
            var Q38;
            Q38=sQuery(id+"F0.wireOp",VERTEX,"E43.3.0.0");
            var Q39;
            Q39=sQuery(id+"F0.wireOp",VERTEX,"E43.2.0.28");
            var Q40;
            Q40=sQuery(id+"F0.wireOp",VERTEX,"E18.MirrorP");
            var Q41;
            Q41=sQuery(id+"F0.wireOp",VERTEX,"E43.2.0.30");
            var Q42;
            Q42=sQuery(id+"F0.wireOp",VERTEX,"E43.1.0.8");
            var Q43;
            Q43=sQuery(id+"F0.wireOp",VERTEX,"E43.1.0.0");
            var Q44;
            Q44=sQuery(id+"F0.wireOp",VERTEX,"E43.3.0.12");
            var Q45;
            Q45=sQuery(id+"F0.wireOp",VERTEX,"E43.4.0.31");
            var Q46;
            Q46=sQuery(id+"F0.wireOp",VERTEX,"E43.4.0.6");
            var Q47;
            Q47=sQuery(id+"F0.wireOp",VERTEX,"E43.4.0.34");
            var Q48;
            Q48=sQuery(id+"F0.wireOp",VERTEX,"E43.1.0.17");
            var Q49;
            Q49=sQuery(id+"F0.wireOp",VERTEX,"E17.MirrorP");
            var Q50;
            Q50=sQuery(id+"F0.wireOp",VERTEX,"E43.1.0.4");
            var Q51;
            Q51=sQuery(id+"F0.wireOp",VERTEX,"E43.1.0.12");
            var Q52;
            Q52=sQuery(id+"F0.wireOp",VERTEX,"E43.1.0.11");
            var Q53;
            Q53=sQuery(id+"F0.wireOp",VERTEX,"E43.4.0.5");
            var Q54;
            Q54=sQuery(id+"F0.wireOp",VERTEX,"E43.3.0.31");
            var Q55;
            Q55=sQuery(id+"F0.wireOp",VERTEX,"E43.2.0.9");
            var Q56;
            Q56=sQuery(id+"F0.wireOp",VERTEX,"E43.1.0.34");
            var Q57;
            Q57=sQuery(id+"F0.wireOp",VERTEX,"E43.3.0.4");
            var Q58;
            Q58=sQuery(id+"F0.wireOp",VERTEX,"E43.3.0.13");
            var Q59;
            Q59=sQuery(id+"F0.wireOp",VERTEX,"E43.4.0.11");
            var Q60;
            Q60=sQuery(id+"F0.wireOp",VERTEX,"E43.2.0.6");
            var Q61;
            Q61=sQuery(id+"F0.wireOp",VERTEX,"E43.2.0.13");
            var Q62;
            Q62=sQuery(id+"F0.wireOp",VERTEX,"E43.3.0.21");
            var Q63;
            Q63=sQuery(id+"F0.wireOp",VERTEX,"E43.2.0.34");
            var Q64;
            Q64=sQuery(id+"F0.wireOp",VERTEX,"E30.MirrorP");
            var Q65;
            Q65=sQuery(id+"F0.wireOp",VERTEX,"E43.1.0.1");
            var Q66;
            Q66=sQuery(id+"F0.wireOp",VERTEX,"E20.MirrorP");
            var Q67;
            Q67=sQuery(id+"F0.wireOp",VERTEX,"E43.1.0.29");
            var Q68;
            Q68=sQuery(id+"F0.wireOp",VERTEX,"E43.2.0.29");
            var Q69;
            Q69=sQuery(id+"F0.wireOp",VERTEX,"E37.MirrorP");
            var Q70;
            Q70=sQuery(id+"F0.wireOp",VERTEX,"E43.2.0.11");
            var Q71;
            Q71=sQuery(id+"F0.wireOp",VERTEX,"E43.4.0.7");
            var Q72;
            Q72=sQuery(id+"F0.wireOp",VERTEX,"E43.4.0.13");
            var Q73;
            Q73=sQuery(id+"F0.wireOp",VERTEX,"E43.2.0.12");
            var Q74;
            Q74=sQuery(id+"F0.wireOp",VERTEX,"E28.MirrorP");
            var Q75;
            Q75=sQuery(id+"F0.wireOp",VERTEX,"E34.MirrorP");
            var Q76;
            Q76=sQuery(id+"F0.wireOp",VERTEX,"E43.4.0.12");
            var Q77;
            Q77=sQuery(id+"F0.wireOp",VERTEX,"E43.4.0.9");
            var Q78;
            Q78=sQuery(id+"F0.wireOp",VERTEX,"E43.4.0.8");
            var Q79;
            Q79=sQuery(id+"F0.wireOp",VERTEX,"E43.2.0.0");
            var Q80;
            Q80=sQuery(id+"F0.wireOp",VERTEX,"E43.1.0.38");
            var Q81;
            Q81=sQuery(id+"F0.wireOp",VERTEX,"E21.MirrorP");
            var Q82;
            Q82=sQuery(id+"F0.wireOp",VERTEX,"E43.4.0.21");
            var Q83;
            Q83=sQuery(id+"F0.wireOp",VERTEX,"E43.4.0.39");
            var Q84;
            Q84=sQuery(id+"F0.wireOp",VERTEX,"E43.4.0.30");
            var Q85;
            Q85=sQuery(id+"F0.wireOp",VERTEX,"E22.MirrorP");
            var Q86;
            Q86=sQuery(id+"F0.wireOp",VERTEX,"E43.2.0.5");
            var Q87;
            Q87=sQuery(id+"F0.wireOp",VERTEX,"E43.3.0.29");
            var Q88;
            Q88=sQuery(id+"F0.wireOp",VERTEX,"E32.MirrorP");
            var Q89;
            Q89=sQuery(id+"F0.wireOp",VERTEX,"E43.3.0.34");
            var Q90;
            Q90=sQuery(id+"F0.wireOp",VERTEX,"E43.2.0.17");
            var Q91;
            Q91=sQuery(id+"F0.wireOp",VERTEX,"E43.3.0.1");
            var Q92;
            Q92=sQuery(id+"F0.wireOp",VERTEX,"E43.2.0.7");
            var Q93;
            Q93=sQuery(id+"F0.wireOp",VERTEX,"E43.1.0.31");
            var Q94;
            Q94=sQuery(id+"F0.wireOp",VERTEX,"E43.4.0.1");
            var Q95;
            Q95=sQuery(id+"F0.wireOp",VERTEX,"E43.1.0.28");
            var Q96;
            Q96=sQuery(id+"F0.wireOp",VERTEX,"E43.4.0.29");
            var Q97;
            Q97=sQuery(id+"F0.wireOp",VERTEX,"E43.1.0.7");
            var Q98;
            Q98=sQuery(id+"F0.wireOp",VERTEX,"E43.3.0.11");
            var Q99;
            Q99=sQuery(id+"F0.wireOp",VERTEX,"E43.3.0.30");
            var Q100;
            Q100=makeQuery(id+"F1.opExtrude","SWEPT_BODY",BODY,{"disambiguationData":[OSD([sQuery(id+"F0.wireOp",EDGE,"E0.bottom"),sQuery(id+"F0.wireOp",EDGE,"E0.top"),sQuery(id+"F0.wireOp",EDGE,"E0.left"),sQuery(id+"F0.wireOp",EDGE,"E0.right"),sQuery(id+"F0.wireOp",EDGE,"E10.0.1.2")])]});
            hole(context, id + "F4", {"style" : HoleStyle.SIMPLE, "endStyle" : HoleEndStyle.THROUGH, "oppositeDirection" : true, "holeDiameter" : 4 * mm, "majorDiameter" : 5 * mm, "isTappedThrough" : true, "tappedDepth" : 26.25 * mm, "tapClearance" : 3, "locations" : qUnion([Q0, Q1, Q2, Q3, Q4, Q5, Q6, Q7, Q8, Q9, Q10, Q11, Q12, Q13, Q14, Q15, Q16, Q17, Q18, Q19, Q20, Q21, Q22, Q23, Q24, Q25, Q26, Q27, Q28, Q29, Q30, Q31, Q32, Q33, Q34, Q35, Q36, Q37, Q38, Q39, Q40, Q41, Q42, Q43, Q44, Q45, Q46, Q47, Q48, Q49, Q50, Q51, Q52, Q53, Q54, Q55, Q56, Q57, Q58, Q59, Q60, Q61, Q62, Q63, Q64, Q65, Q66, Q67, Q68, Q69, Q70, Q71, Q72, Q73, Q74, Q75, Q76, Q77, Q78, Q79, Q80, Q81, Q82, Q83, Q84, Q85, Q86, Q87, Q88, Q89, Q90, Q91, Q92, Q93, Q94, Q95, Q96, Q97, Q98, Q99]), "scope" : qUnion([Q100])});
        }
        {
            var Q0;
            Q0=sQuery(id+"F0.wireOp",VERTEX,"E43.3.0.2");
            var Q1;
            Q1=sQuery(id+"F0.wireOp",VERTEX,"E43.1.0.10");
            var Q2;
            Q2=sQuery(id+"F0.wireOp",VERTEX,"E43.1.0.36");
            var Q3;
            Q3=sQuery(id+"F0.wireOp",VERTEX,"E43.4.0.23");
            var Q4;
            Q4=sQuery(id+"F0.wireOp",VERTEX,"E43.4.0.24");
            var Q5;
            Q5=sQuery(id+"F0.wireOp",VERTEX,"E43.3.0.18");
            var Q6;
            Q6=sQuery(id+"F0.wireOp",VERTEX,"E43.3.0.37");
            var Q7;
            Q7=sQuery(id+"F0.wireOp",VERTEX,"E43.1.0.2");
            var Q8;
            Q8=sQuery(id+"F0.wireOp",VERTEX,"E43.4.0.2");
            var Q9;
            Q9=sQuery(id+"F0.wireOp",VERTEX,"E43.3.0.16");
            var Q10;
            Q10=sQuery(id+"F0.wireOp",VERTEX,"E43.2.0.33");
            var Q11;
            Q11=sQuery(id+"F0.wireOp",VERTEX,"E43.1.0.26");
            var Q12;
            Q12=sQuery(id+"F0.wireOp",VERTEX,"E43.2.0.20");
            var Q13;
            Q13=sQuery(id+"F0.wireOp",VERTEX,"E43.2.0.36");
            var Q14;
            Q14=sQuery(id+"F0.wireOp",VERTEX,"E43.2.0.18");
            var Q15;
            Q15=sQuery(id+"F0.wireOp",VERTEX,"E23.MirrorP");
            var Q16;
            Q16=sQuery(id+"F0.wireOp",VERTEX,"E26.MirrorP");
            var Q17;
            Q17=sQuery(id+"F0.wireOp",VERTEX,"E43.1.0.16");
            var Q18;
            Q18=sQuery(id+"F0.wireOp",VERTEX,"E43.2.0.10");
            var Q19;
            Q19=sQuery(id+"F0.wireOp",VERTEX,"E43.3.0.32");
            var Q20;
            Q20=sQuery(id+"F0.wireOp",VERTEX,"E43.4.0.35");
            var Q21;
            Q21=sQuery(id+"F0.wireOp",VERTEX,"E43.1.0.22");
            var Q22;
            Q22=sQuery(id+"F0.wireOp",VERTEX,"E43.3.0.35");
            var Q23;
            Q23=sQuery(id+"F0.wireOp",VERTEX,"E43.3.0.33");
            var Q24;
            Q24=sQuery(id+"F0.wireOp",VERTEX,"E43.4.0.37");
            var Q25;
            Q25=sQuery(id+"F0.wireOp",VERTEX,"E43.1.0.37");
            var Q26;
            Q26=sQuery(id+"F0.wireOp",VERTEX,"E43.1.0.32");
            var Q27;
            Q27=sQuery(id+"F0.wireOp",VERTEX,"E43.3.0.15");
            var Q28;
            Q28=sQuery(id+"F0.wireOp",VERTEX,"E43.4.0.33");
            var Q29;
            Q29=sQuery(id+"F0.wireOp",VERTEX,"E43.1.0.24");
            var Q30;
            Q30=sQuery(id+"F0.wireOp",VERTEX,"E43.1.0.18");
            var Q31;
            Q31=sQuery(id+"F0.wireOp",VERTEX,"E43.2.0.32");
            var Q32;
            Q32=sQuery(id+"F0.wireOp",VERTEX,"E43.1.0.33");
            var Q33;
            Q33=sQuery(id+"F0.wireOp",VERTEX,"E43.3.0.20");
            var Q34;
            Q34=sQuery(id+"F0.wireOp",VERTEX,"E43.1.0.35");
            var Q35;
            Q35=sQuery(id+"F0.wireOp",VERTEX,"E43.2.0.14");
            var Q36;
            Q36=sQuery(id+"F0.wireOp",VERTEX,"E43.2.0.37");
            var Q37;
            Q37=sQuery(id+"F0.wireOp",VERTEX,"E43.2.0.23");
            var Q38;
            Q38=sQuery(id+"F0.wireOp",VERTEX,"E43.1.0.14");
            var Q39;
            Q39=sQuery(id+"F0.wireOp",VERTEX,"E43.2.0.16");
            var Q40;
            Q40=sQuery(id+"F0.wireOp",VERTEX,"E43.3.0.22");
            var Q41;
            Q41=sQuery(id+"F0.wireOp",VERTEX,"E43.1.0.15");
            var Q42;
            Q42=sQuery(id+"F0.wireOp",VERTEX,"E43.2.0.15");
            var Q43;
            Q43=sQuery(id+"F0.wireOp",VERTEX,"E43.4.0.16");
            var Q44;
            Q44=sQuery(id+"F0.wireOp",VERTEX,"E40.MirrorP");
            var Q45;
            Q45=sQuery(id+"F0.wireOp",VERTEX,"E43.2.0.24");
            var Q46;
            Q46=sQuery(id+"F0.wireOp",VERTEX,"E43.3.0.23");
            var Q47;
            Q47=sQuery(id+"F0.wireOp",VERTEX,"E43.3.0.14");
            var Q48;
            Q48=sQuery(id+"F0.wireOp",VERTEX,"E43.1.0.20");
            var Q49;
            Q49=sQuery(id+"F0.wireOp",VERTEX,"E43.4.0.20");
            var Q50;
            Q50=sQuery(id+"F0.wireOp",VERTEX,"E43.2.0.26");
            var Q51;
            Q51=sQuery(id+"F0.wireOp",VERTEX,"E43.1.0.23");
            var Q52;
            Q52=sQuery(id+"F0.wireOp",VERTEX,"E24.MirrorP");
            var Q53;
            Q53=sQuery(id+"F0.wireOp",VERTEX,"E43.3.0.26");
            var Q54;
            Q54=sQuery(id+"F0.wireOp",VERTEX,"E31.MirrorP");
            var Q55;
            Q55=sQuery(id+"F0.wireOp",VERTEX,"E43.3.0.36");
            var Q56;
            Q56=sQuery(id+"F0.wireOp",VERTEX,"E25.MirrorP");
            var Q57;
            Q57=sQuery(id+"F0.wireOp",VERTEX,"E41.MirrorP");
            var Q58;
            Q58=sQuery(id+"F0.wireOp",VERTEX,"E43.2.0.35");
            var Q59;
            Q59=sQuery(id+"F0.wireOp",VERTEX,"E43.4.0.26");
            var Q60;
            Q60=sQuery(id+"F0.wireOp",VERTEX,"E43.4.0.18");
            var Q61;
            Q61=sQuery(id+"F0.wireOp",VERTEX,"E43.4.0.32");
            var Q62;
            Q62=sQuery(id+"F0.wireOp",VERTEX,"E43.2.0.22");
            var Q63;
            Q63=sQuery(id+"F0.wireOp",VERTEX,"E43.4.0.15");
            var Q64;
            Q64=sQuery(id+"F0.wireOp",VERTEX,"E43.3.0.10");
            var Q65;
            Q65=sQuery(id+"F0.wireOp",VERTEX,"E43.3.0.24");
            var Q66;
            Q66=sQuery(id+"F0.wireOp",VERTEX,"E43.2.0.2");
            var Q67;
            Q67=sQuery(id+"F0.wireOp",VERTEX,"E43.4.0.14");
            var Q68;
            Q68=sQuery(id+"F0.wireOp",VERTEX,"E43.4.0.22");
            var Q69;
            Q69=sQuery(id+"F0.wireOp",VERTEX,"E43.4.0.36");
            var Q70;
            Q70=sQuery(id+"F0.wireOp",VERTEX,"E27.MirrorP");
            var Q71;
            Q71=sQuery(id+"F0.wireOp",VERTEX,"E43.4.0.10");
            var Q72;
            Q72=sQuery(id+"F0.wireOp",VERTEX,"E10.0.1.3");
            var Q73;
            Q73=sQuery(id+"F0.wireOp",VERTEX,"E10.0.1.5");
            var Q74;
            Q74=sQuery(id+"F0.wireOp",VERTEX,"E3");
            var Q75;
            Q75=sQuery(id+"F0.wireOp",VERTEX,"E1");
            var Q76;
            Q76=sQuery(id+"F0.wireOp",VERTEX,"E2");
            var Q77;
            Q77=sQuery(id+"F0.wireOp",VERTEX,"E10.0.1.6");
            var Q78;
            Q78=sQuery(id+"F0.wireOp",VERTEX,"E4");
            var Q79;
            Q79=sQuery(id+"F0.wireOp",VERTEX,"E10.0.1.4");
            var Q80;
            Q80=makeQuery(id+"F1.opExtrude","SWEPT_BODY",BODY,{"disambiguationData":[OSD([sQuery(id+"F0.wireOp",EDGE,"E0.bottom"),sQuery(id+"F0.wireOp",EDGE,"E0.top"),sQuery(id+"F0.wireOp",EDGE,"E0.left"),sQuery(id+"F0.wireOp",EDGE,"E0.right"),sQuery(id+"F0.wireOp",EDGE,"E10.0.1.2")])]});
            hole(context, id + "F5", {"style" : HoleStyle.SIMPLE, "endStyle" : HoleEndStyle.THROUGH, "oppositeDirection" : true, "holeDiameter" : 4 * mm, "majorDiameter" : 5 * mm, "isTappedThrough" : true, "tappedDepth" : 26.25 * mm, "tapClearance" : 3, "locations" : qUnion([Q0, Q1, Q2, Q3, Q4, Q5, Q6, Q7, Q8, Q9, Q10, Q11, Q12, Q13, Q14, Q15, Q16, Q17, Q18, Q19, Q20, Q21, Q22, Q23, Q24, Q25, Q26, Q27, Q28, Q29, Q30, Q31, Q32, Q33, Q34, Q35, Q36, Q37, Q38, Q39, Q40, Q41, Q42, Q43, Q44, Q45, Q46, Q47, Q48, Q49, Q50, Q51, Q52, Q53, Q54, Q55, Q56, Q57, Q58, Q59, Q60, Q61, Q62, Q63, Q64, Q65, Q66, Q67, Q68, Q69, Q70, Q71, Q72, Q73, Q74, Q75, Q76, Q77, Q78, Q79]), "scope" : qUnion([Q80])});
        }
        {
            var Q0;
            Q0=sQuery(id+"F0.wireOp",VERTEX,"E11.MirrorP");
            var Q1;
            Q1=sQuery(id+"F0.wireOp",VERTEX,"E43.2.0.3");
            var Q2;
            Q2=sQuery(id+"F0.wireOp",VERTEX,"E43.2.0.25");
            var Q3;
            Q3=sQuery(id+"F0.wireOp",VERTEX,"E43.1.0.25");
            var Q4;
            Q4=sQuery(id+"F0.wireOp",VERTEX,"E43.3.0.3");
            var Q5;
            Q5=sQuery(id+"F0.wireOp",VERTEX,"E43.1.0.3");
            var Q6;
            Q6=sQuery(id+"F0.wireOp",VERTEX,"E43.4.0.3");
            var Q7;
            Q7=sQuery(id+"F0.wireOp",VERTEX,"E43.4.0.25");
            var Q8;
            Q8=sQuery(id+"F0.wireOp",VERTEX,"E43.4.0.27");
            var Q9;
            Q9=sQuery(id+"F0.wireOp",VERTEX,"E29.MirrorP");
            var Q10;
            Q10=sQuery(id+"F0.wireOp",VERTEX,"E43.2.0.19");
            var Q11;
            Q11=sQuery(id+"F0.wireOp",VERTEX,"E43.1.0.19");
            var Q12;
            Q12=sQuery(id+"F0.wireOp",VERTEX,"E14.MirrorP");
            var Q13;
            Q13=sQuery(id+"F0.wireOp",VERTEX,"E43.3.0.25");
            var Q14;
            Q14=sQuery(id+"F0.wireOp",VERTEX,"E43.1.0.27");
            var Q15;
            Q15=sQuery(id+"F0.wireOp",VERTEX,"E43.2.0.27");
            var Q16;
            Q16=sQuery(id+"F0.wireOp",VERTEX,"E43.3.0.27");
            var Q17;
            Q17=sQuery(id+"F0.wireOp",VERTEX,"E43.3.0.19");
            var Q18;
            Q18=sQuery(id+"F0.wireOp",VERTEX,"E39.MirrorP");
            var Q19;
            Q19=sQuery(id+"F0.wireOp",VERTEX,"E43.4.0.19");
            var Q20;
            Q20=makeQuery(id+"F1.opExtrude","SWEPT_BODY",BODY,{"disambiguationData":[OSD([sQuery(id+"F0.wireOp",EDGE,"E0.bottom"),sQuery(id+"F0.wireOp",EDGE,"E0.top"),sQuery(id+"F0.wireOp",EDGE,"E0.left"),sQuery(id+"F0.wireOp",EDGE,"E0.right"),sQuery(id+"F0.wireOp",EDGE,"E10.0.1.2")])]});
            hole(context, id + "F6", {"style" : HoleStyle.SIMPLE, "endStyle" : HoleEndStyle.THROUGH, "oppositeDirection" : true, "holeDiameter" : 4 * mm, "majorDiameter" : 5 * mm, "isTappedThrough" : true, "tappedDepth" : 26.25 * mm, "tapClearance" : 3, "locations" : qUnion([Q0, Q1, Q2, Q3, Q4, Q5, Q6, Q7, Q8, Q9, Q10, Q11, Q12, Q13, Q14, Q15, Q16, Q17, Q18, Q19]), "scope" : qUnion([Q20])});
        }
        {
            var Q0;
            Q0=makeQuery(id+"F1.opExtrude","CAP_FACE",FACE,{"disambiguationData":[OSD([sQuery(id+"F0.wireOp",EDGE,"E0.bottom"),sQuery(id+"F0.wireOp",EDGE,"E0.top"),sQuery(id+"F0.wireOp",EDGE,"E0.left"),sQuery(id+"F0.wireOp",EDGE,"E0.right"),sQuery(id+"F0.wireOp",EDGE,"E10.0.1.2")])],"isStart":true});
            var sketch = newSketch(context, id + "F7", { "sketchPlane" : qUnion([Q0])});
            skLineSegment(sketch, "E165.0", {"start": v(-25, -390) * mm, "end": v(-700, -390) * mm});
            skLineSegment(sketch, "E165.1", {"start": v(-5, -25) * mm, "end": v(-5, -370) * mm});
            skLineSegment(sketch, "E165.2", {"start": v(-25, -5) * mm, "end": v(-700, -5) * mm});
            skPoint(sketch, "E166.visualSharp", {"position": v(-5, -390) * mm});
            skArc(sketch, "E166.filletArc", {"start": v(-25, -390) * mm, "mid": v(-10.86, -384.14) * mm, "end": v(-5, -370) * mm});
            skPoint(sketch, "E167.visualSharp", {"position": v(-5, -5) * mm});
            skArc(sketch, "E167.filletArc", {"start": v(-5, -25) * mm, "mid": v(-10.86, -10.86) * mm, "end": v(-25, -5) * mm});
            skLineSegment(sketch, "E168", {"start": v(-700, -390) * mm, "end": v(-700, -5) * mm});
            skSolve(sketch);
        }
        {
            var Q0;
            Q0 = qSketchRegion(id + "F7", true);
            var Q1;
            Q1=makeQuery(id+"F1.opExtrude","CAP_FACE",FACE,{"disambiguationData":[OSD([sQuery(id+"F0.wireOp",EDGE,"E0.bottom"),sQuery(id+"F0.wireOp",EDGE,"E0.top"),sQuery(id+"F0.wireOp",EDGE,"E0.left"),sQuery(id+"F0.wireOp",EDGE,"E0.right"),sQuery(id+"F0.wireOp",EDGE,"E10.0.1.2")])],"isStart":false});
            extrude(context, id + "F8", {"entities" : qUnion([Q0, Q1]), "operationType" : NewBodyOperationType.REMOVE, "oppositeDirection" : true, "depth" : 4.46 * mm, "offsetDistance" : 25 * mm});
        }
    });
